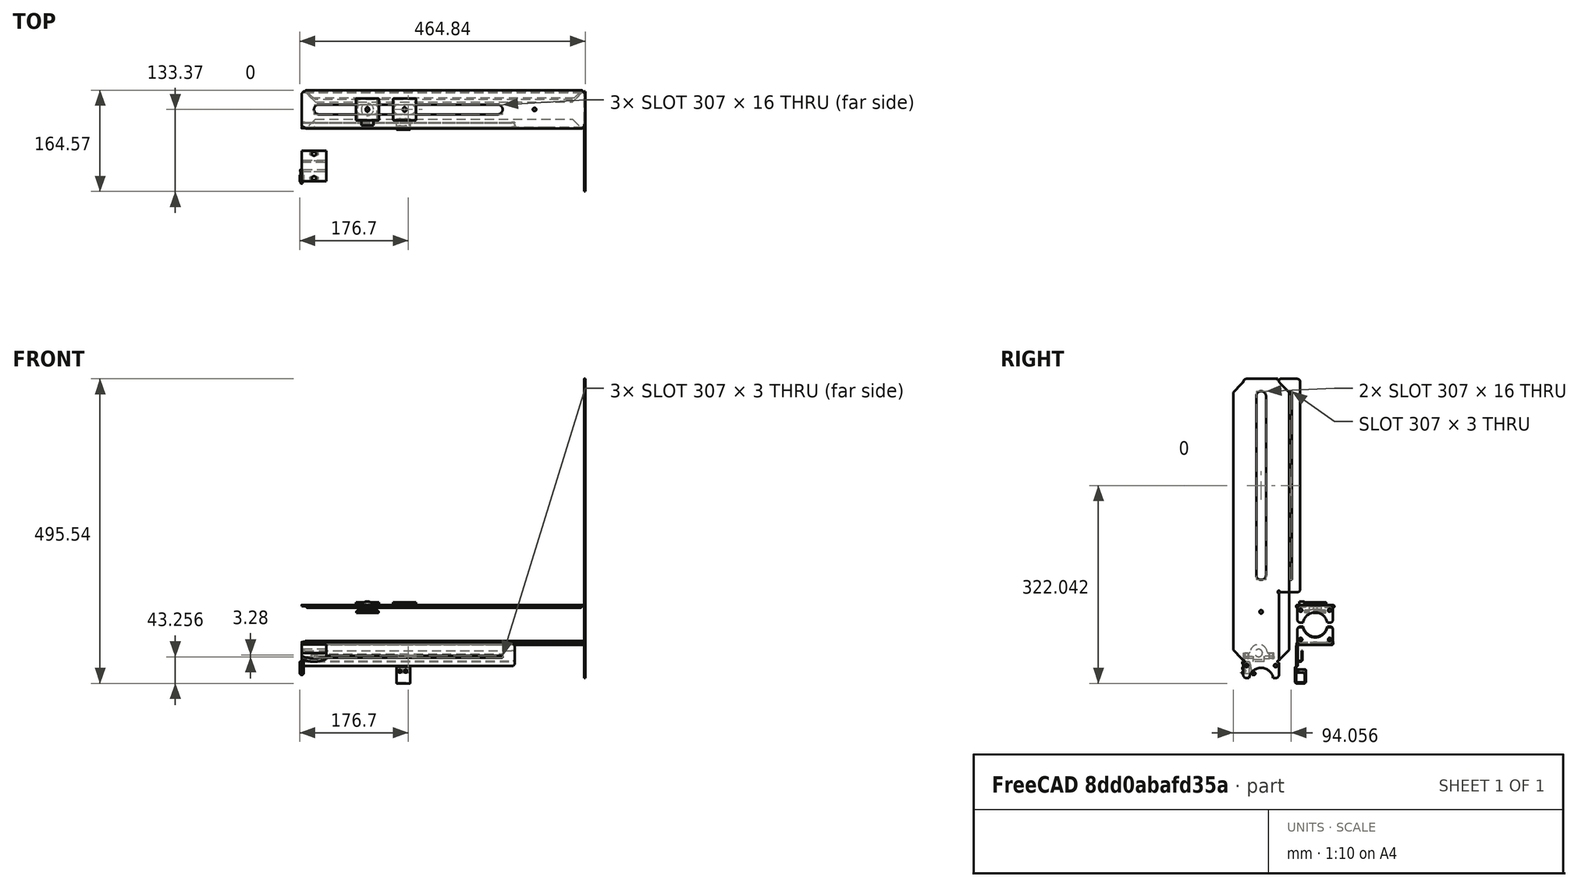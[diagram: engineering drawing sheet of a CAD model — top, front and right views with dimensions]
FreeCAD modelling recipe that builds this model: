
FCSTD DOCUMENT  (FreeCAD 1.0R39285 (Git))
Label: Heberteile
License: All rights reserved
LicenseURL: https://en.wikipedia.org/wiki/All_rights_reserved
objects: Sketcher::SketchObject×33, TechDraw::DrawViewDimension×24, PartDesign::FeaturePython×14, PartDesign::Body×9, PartDesign::Pad×9, Part::Feature×7, PartDesign::Pocket×6, Mesh::Feature×6, TechDraw::DrawProjGroupItem×4, App::DocumentObjectGroup×4, PartDesign::Chamfer×3, PartDesign::Fillet×3, Part::FeaturePython×2, TechDraw::DrawSVGTemplate×2, TechDraw::DrawPage×2, TechDraw::DrawViewImage×1, App::Part×1, PartDesign::Hole×1, PartDesign::SubtractiveLoft×1
note: 223 computed .brp shape members not serialized (recipe doc carries the construction recipe); baked Part::Feature solids carry a one-line shape summary decoded from their .brp

FEATURE [Sketcher::SketchObject] Sketch  label="Sk-Steppersledge-Switch_base"
  ArcFitTolerance = 1e-06
  AttachmentSupport = -> [XY_Plane]
  FullyConstrained = true
  MakeInternals = false
  MapMode = 5
  sketch-geometry (83):
    g0: Circle CenterX=379 CenterY=29 CenterZ=0 NormalX=0 NormalY=0 NormalZ=1 AngleXU=0 Radius=2.75
    g1: ArcOfCircle CenterX=28 CenterY=29 CenterZ=0 NormalX=0 NormalY=0 NormalZ=1 AngleXU=0 Radius=8 StartAngle=1.5708 EndAngle=4.71239
    g2: ArcOfCircle CenterX=319 CenterY=29 CenterZ=0 NormalX=0 NormalY=0 NormalZ=1 AngleXU=0 Radius=8 StartAngle=4.71239 EndAngle=7.85398
    g3: LineSegment StartX=28 StartY=37 StartZ=0 EndX=319 EndY=37 EndZ=0
    g4: LineSegment StartX=28 StartY=21 StartZ=0 EndX=319 EndY=21 EndZ=0
    g5: GeomPoint [constr] X=0 Y=58 Z=0
    g6: ArcOfCircle CenterX=5 CenterY=5 CenterZ=0 NormalX=0 NormalY=0 NormalZ=1 AngleXU=0 Radius=5 StartAngle=3.14159 EndAngle=4.71239
    g7: GeomPoint [constr] X=0 Y=0 Z=0
    g8: LineSegment StartX=487 StartY=48.6914 StartZ=0 EndX=487 EndY=53 EndZ=0
    g9: LineSegment StartX=487 StartY=5 StartZ=0 EndX=487 EndY=9.30863 EndZ=0
    g10: LineSegment [constr] StartX=487 StartY=9.30863 StartZ=0 EndX=487 EndY=48.6914 EndZ=0
    g11: ArcOfCircle CenterX=490.5 CenterY=29 CenterZ=0 NormalX=0 NormalY=0 NormalZ=1 AngleXU=0 Radius=20 StartAngle=1.7467 EndAngle=4.53648
    g12: LineSegment [constr] StartX=490.5 StartY=29 StartZ=0 EndX=487 EndY=29 EndZ=0
    g13: GeomPoint X=20 Y=29 Z=0
    g14: LineSegment StartX=0 StartY=56 StartZ=0 EndX=0 EndY=29 EndZ=0
    g15: LineSegment StartX=0 StartY=29 StartZ=0 EndX=0 EndY=5 EndZ=0
    g16: LineSegment [constr] StartX=460 StartY=58 StartZ=0 EndX=460 EndY=0 EndZ=0
    g17: LineSegment [constr] StartX=490.5 StartY=52.57 StartZ=0 EndX=466.93 EndY=52.57 EndZ=0
    g18: LineSegment [constr] StartX=490.5 StartY=5.43 StartZ=0 EndX=466.93 EndY=5.43 EndZ=0
    g19: LineSegment [constr] StartX=466.93 StartY=52.57 StartZ=0 EndX=466.93 EndY=5.43 EndZ=0
    g20: LineSegment [constr] StartX=490.5 StartY=52.57 StartZ=0 EndX=490.5 EndY=29 EndZ=0
    g21: LineSegment [constr] StartX=490.5 StartY=29 StartZ=0 EndX=490.5 EndY=5.43 EndZ=0
    g22: ArcOfCircle CenterX=482 CenterY=53 CenterZ=0 NormalX=0 NormalY=0 NormalZ=1 AngleXU=0 Radius=5 StartAngle=0 EndAngle=1.5708
    g23: GeomPoint [constr] X=487 Y=58 Z=0
    g24: ArcOfCircle CenterX=482 CenterY=5 CenterZ=0 NormalX=0 NormalY=0 NormalZ=1 AngleXU=0 Radius=5 StartAngle=4.71239 EndAngle=6.28319
    g25: GeomPoint [constr] X=487 Y=0 Z=0
    g26: Circle CenterX=466.93 CenterY=52.57 CenterZ=0 NormalX=0 NormalY=0 NormalZ=1 AngleXU=0 Radius=2.6
    g27: Circle CenterX=466.93 CenterY=5.43 CenterZ=0 NormalX=0 NormalY=0 NormalZ=1 AngleXU=0 Radius=2.6
    g28: LineSegment [constr] StartX=462.83 StartY=50.2029 StartZ=0 EndX=466.93 EndY=47.8357 EndZ=0
    g29: LineSegment [constr] StartX=466.93 StartY=47.8357 StartZ=0 EndX=471.03 EndY=50.2029 EndZ=0
    g30: LineSegment [constr] StartX=471.03 StartY=50.2029 StartZ=0 EndX=471.03 EndY=54.9371 EndZ=0
    g31: LineSegment [constr] StartX=471.03 StartY=54.9371 StartZ=0 EndX=466.93 EndY=57.3043 EndZ=0
    g32: LineSegment [constr] StartX=466.93 StartY=57.3043 StartZ=0 EndX=462.83 EndY=54.9371 EndZ=0
    g33: LineSegment [constr] StartX=462.83 StartY=54.9371 StartZ=0 EndX=462.83 EndY=50.2029 EndZ=0
    g34: Circle [constr] CenterX=466.93 CenterY=52.57 CenterZ=0 NormalX=0 NormalY=0 NormalZ=1 AngleXU=0 Radius=4.73427
    g35: LineSegment StartX=458 StartY=58 StartZ=0 EndX=400 EndY=58 EndZ=0
    g36: LineSegment StartX=482 StartY=58 StartZ=0 EndX=462 EndY=58 EndZ=0
    g37: LineSegment [constr] StartX=462 StartY=58 StartZ=0 EndX=458 EndY=58 EndZ=0
    g38: ArcOfCircle CenterX=460 CenterY=58 CenterZ=0 NormalX=0 NormalY=0 NormalZ=1 AngleXU=0 Radius=2 StartAngle=3.14159 EndAngle=6.28319
    g39: LineSegment StartX=462 StartY=0 StartZ=0 EndX=482 EndY=0 EndZ=0
    g40: LineSegment [constr] StartX=5 StartY=0 StartZ=0 EndX=458 EndY=0 EndZ=0
    g41: LineSegment [constr] StartX=458 StartY=0 StartZ=0 EndX=462 EndY=0 EndZ=0
    g42: ArcOfCircle CenterX=460 CenterY=0 CenterZ=0 NormalX=0 NormalY=0 NormalZ=1 AngleXU=0 Radius=2 StartAngle=0 EndAngle=3.14159
    g43: LineSegment StartX=22 StartY=-17 StartZ=0 EndX=441 EndY=-17 EndZ=0
    g44: LineSegment StartX=441 StartY=-17 StartZ=0 EndX=458 EndY=0 EndZ=0
    g45: LineSegment StartX=22 StartY=-17 StartZ=0 EndX=5 EndY=0 EndZ=0
    g46: LineSegment [constr] StartX=0 StartY=56 StartZ=0 EndX=0 EndY=60 EndZ=0
    g47: LineSegment StartX=5 StartY=93 StartZ=0 EndX=342 EndY=93 EndZ=0
    g48: ArcOfCircle CenterX=5 CenterY=88 CenterZ=0 NormalX=0 NormalY=0 NormalZ=1 AngleXU=0 Radius=5 StartAngle=1.5708 EndAngle=3.14159
    g49: GeomPoint [constr] X=0 Y=93 Z=0
    g50: ArcOfCircle CenterX=342 CenterY=88 CenterZ=0 NormalX=0 NormalY=0 NormalZ=1 AngleXU=0 Radius=5 StartAngle=4e-16 EndAngle=1.5708
    g51: LineSegment StartX=400 StartY=58 StartZ=0 EndX=349 EndY=58 EndZ=0
    g52: LineSegment [constr] StartX=349 StartY=58 StartZ=0 EndX=347 EndY=58 EndZ=0
    g53: ArcOfCircle CenterX=0 CenterY=58 CenterZ=0 NormalX=0 NormalY=0 NormalZ=1 AngleXU=0 Radius=2 StartAngle=4.71239 EndAngle=7.85398
    g54: LineSegment [constr] StartX=347 StartY=60 StartZ=0 EndX=347 EndY=58 EndZ=0
    g55: GeomPoint [constr] X=327 Y=29 Z=0
    g56: LineSegment [constr] StartX=327 StartY=29 StartZ=0 EndX=347 EndY=29 EndZ=0
    g57: LineSegment [constr] StartX=347 StartY=29 StartZ=0 EndX=347 EndY=58 EndZ=0
    g58: LineSegment [constr] StartX=0 StartY=29 StartZ=0 EndX=20 EndY=29 EndZ=0
    g59: LineSegment [constr] StartX=487 StartY=29 StartZ=0 EndX=460 EndY=29 EndZ=0
    g60: LineSegment [constr] StartX=460 StartY=29 StartZ=0 EndX=400 EndY=29 EndZ=0
    g61: LineSegment [constr] StartX=400 StartY=29 StartZ=0 EndX=379 EndY=29 EndZ=0
    g62: LineSegment [constr] StartX=379 StartY=29 StartZ=0 EndX=347 EndY=29 EndZ=0
    g63: LineSegment [constr] StartX=327 StartY=29 StartZ=0 EndX=20 EndY=29 EndZ=0
    g64: LineSegment [constr] StartX=400 StartY=58 StartZ=0 EndX=400 EndY=29 EndZ=0
    g65: LineSegment [constr] StartX=400 StartY=29 StartZ=0 EndX=400 EndY=0 EndZ=0
    g66: LineSegment [constr] StartX=0 StartY=58 StartZ=0 EndX=347 EndY=58 EndZ=0
    g67: ArcOfCircle CenterX=347 CenterY=58 CenterZ=0 NormalX=0 NormalY=0 NormalZ=1 AngleXU=0 Radius=2 StartAngle=1.5708 EndAngle=6.28319
    g68: LineSegment [constr] StartX=28 StartY=29 StartZ=0 EndX=28 EndY=58 EndZ=0
    g69: LineSegment [constr] StartX=28 StartY=58 StartZ=0 EndX=28 EndY=78 EndZ=0
    g70: LineSegment [constr] StartX=28 StartY=78 StartZ=0 EndX=28 EndY=88 EndZ=0
    g71: LineSegment StartX=0 StartY=60 StartZ=0 EndX=0 EndY=88 EndZ=0
    g72: LineSegment StartX=347 StartY=88 StartZ=0 EndX=347 EndY=60 EndZ=0
    g73: LineSegment [constr] StartX=0 StartY=88 StartZ=0 EndX=347 EndY=88 EndZ=0
    g74: LineSegment [constr] StartX=0 StartY=78 StartZ=0 EndX=347 EndY=78 EndZ=0
    g75: ArcOfCircle CenterX=21.5 CenterY=78 CenterZ=0 NormalX=0 NormalY=0 NormalZ=1 AngleXU=0 Radius=1.5 StartAngle=1.5708 EndAngle=4.71239
    g76: ArcOfCircle CenterX=325.5 CenterY=78 CenterZ=0 NormalX=0 NormalY=0 NormalZ=1 AngleXU=0 Radius=1.5 StartAngle=4.71239 EndAngle=7.85398
    g77: LineSegment StartX=21.5 StartY=79.5 StartZ=0 EndX=325.5 EndY=79.5 EndZ=0
    g78: LineSegment StartX=21.5 StartY=76.5 StartZ=0 EndX=325.5 EndY=76.5 EndZ=0
    g79: GeomPoint X=327 Y=78 Z=0
    g80: GeomPoint X=20 Y=78 Z=0
    g81: LineSegment [constr] StartX=20 StartY=78 StartZ=0 EndX=20 EndY=29 EndZ=0
    g82: LineSegment [constr] StartX=327 StartY=78 StartZ=0 EndX=327 EndY=29 EndZ=0
  constraints (211):
    c: Diameter(g0) = 5.5
    c: Tangent(g1,g3) = 1.5708
    c: Tangent(g1,g4) = -1.5708
    c: Tangent(g2,g3) = 1.5708
    c: Tangent(g2,g4) = -1.5708
    c: Equal(g1,g2)
    c: Horizontal(g4)
    c: Coincident(g35,g51)
    c: DistanceY(g65,g64) = 58
    c: Coincident(g35,g64)
    c: Coincident(g10,g8)
    c: Vertical(g8)
    c: Coincident(g9,g10)
    c: Vertical(g9)
    c: Vertical(g10)
    c: Coincident(g11,g8)
    c: Coincident(g11,g9)
    c: Coincident(g12,g11)
    c: Horizontal(g12)
    c: Radius(g11) = 20
    c: DistanceX(g12,g12) = 3.5
    c: DistanceX(g15,g65) = 400
    c: Coincident(g14,g15)
    c: PointOnObject(g7,g14)
    c: DistanceX(g14,g13) = 20
    c: Vertical(g14)
    c: Tangent(g15,g6) = -1.5708
    c: Vertical(g15)
    c: DistanceX(g0,g65) = 21
    c: DistanceX(g2,g0) = 60
    c: Vertical(g16)
    c: DistanceX(g65,g16) = 60
    c: Coincident(g17,g20)
    c: Horizontal(g17)
    c: Coincident(g18,g21)
    c: Horizontal(g18)
    c: Coincident(g19,g17)
    c: Coincident(g19,g18)
    c: Vertical(g19)
    c: Coincident(g20,g21)
    c: Vertical(g20)
    c: Vertical(g21)
    c: Equal(g20,g21)
    c: DistanceY(g18,g17) = 47.14
    c: Equal(g20,g17)
    c: PointOnObject(g23,g8)
    c: Tangent(g8,g22) = -1.5708
    c: PointOnObject(g25,g9)
    c: Tangent(g9,g24) = -1.5708
    c: Equal(g24,g22)
    c: DistanceX(g16,g18) = 30.5
    c: Coincident(g26,g17)
    c: Diameter(g26) = 5.2
    c: Coincident(g27,g18)
    c: Equal(g26,g27)
    c: Coincident(g28,g29)
    c: Coincident(g29,g30)
    c: Coincident(g30,g31)
    c: Coincident(g31,g32)
    c: Coincident(g32,g33)
    c: Coincident(g33,g28)
    c: Equal(g28, g29-g33) x5
    c: PointOnObject(g28,g34)
    c: PointOnObject(g29,g34)
    c: PointOnObject(g30,g34)
    c: PointOnObject(g31,g34)
    c: PointOnObject(g32,g34)
    c: PointOnObject(g33,g34)
    c: Coincident(g34,g17)
    c: Vertical(g33)
    c: DistanceX(g32,g30) = 8.2
    c: Radius(g2) = 8
    c: Coincident(g37,g35)
    c: Horizontal(g35)
    c: Coincident(g36,g37)
    c: Horizontal(g36)
    c: Horizontal(g37)
    c: PointOnObject(g16,g36)
    c: PointOnObject(g23,g36)
    c: Coincident(g38,g16)
    c: Coincident(g38,g35)
    c: Coincident(g38,g36)
    c: Radius(g38) = 2
    c: Tangent(g36,g22) = -1.5708
    c: Coincident(g41,g39)
    c: Horizontal(g39)
    c: PointOnObject(g65,g39)
    c: PointOnObject(g16,g39)
    c: PointOnObject(g25,g39)
    c: Coincident(g40,g41)
    c: Horizontal(g40)
    c: Horizontal(g41)
    c: PointOnObject(g7,g40)
    c: Coincident(g42,g16)
    c: Coincident(g42,g39)
    c: Coincident(g42,g40)
    c: Tangent(g39,g24) = -1.5708
    c: Equal(g42,g38)
    c: Tangent(g40,g6) = -1.5708
    c: Horizontal(g43)
    c: Coincident(g43,g44)
    c: Coincident(g44,g40)
    c: Coincident(g45,g43)
    c: Coincident(g45,g6)
    c: Angle(g45,g40) = 0.785398
    c: Equal(g45,g44)
    c: DistanceY(g43,g6) = 17
    c: Vertical(g46)
    c: Coincident(g46,g71)
    c: Horizontal(g47)
    c: Radius(g6) = 5
    c: PointOnObject(g49,g47)
    c: Tangent(g47,g48) = 1.5708
    c: Tangent(g47,g50) = 1.5708
    c: Coincident(g51,g52)
    c: Horizontal(g51)
    c: Horizontal(g52)
    c: Equal(g6,g48)
    c: Equal(g48,g50)
    c: Coincident(g14,g46)
    c: Coincident(g53,g5)
    c: Coincident(g53,g14)
    c: Coincident(g53,g46)
    c: Coincident(g56,g55)
    c: Coincident(g57,g56)
    c: Vertical(g57)
    c: Coincident(g58,g14)
    c: Coincident(g58,g13)
    c: Equal(g58,g56)
    c: PointOnObject(g5,g46)
    c: Horizontal(g56)
    c: Coincident(g11,g20)
    c: Coincident(g59,g12)
    c: PointOnObject(g59,g16)
    c: Horizontal(g59)
    c: Coincident(g60,g59)
    c: Horizontal(g60)
    c: Coincident(g61,g60)
    c: Coincident(g61,g0)
    c: Coincident(g62,g0)
    c: Coincident(g62,g56)
    c: Horizontal(g62)
    c: Horizontal(g61)
    c: Coincident(g63,g55)
    c: PointOnObject(g63,g1)
    c: Horizontal(g63)
    c: Coincident(g13,g63)
    c: PointOnObject(g1,g63)
    c: Horizontal(g58)
    c: PointOnObject(g55,g2)
    c: PointOnObject(g12,g10)
    c: Coincident(g64,g65)
    c: Vertical(g64)
    c: Vertical(g65)
    c: Coincident(g64,g60)
    c: Equal(g64,g65)
    c: Equal(g24,g6)
    c: Coincident(g66,g5)
    c: Horizontal(g66)
    c: Vertical(g54)
    c: Coincident(g57,g54)
    c: Coincident(g52,g54)
    c: Coincident(g72,g54)
    c: Coincident(g66,g52)
    c: Coincident(g67,g52)
    c: Coincident(g67,g54)
    c: Coincident(g67,g51)
    c: Equal(g53,g67)
    c: Equal(g67,g38)
    c: Coincident(g7,g-1)
    c: Coincident(g68,g1)
    c: PointOnObject(g68,g66)
    c: Vertical(g68)
    c: Coincident(g69,g68)
    c: Vertical(g69)
    c: Coincident(g70,g69)
    c: Vertical(g70)
    c: DistanceY(g69,g69) = 20
    c: DistanceY(g70,g70) = 10
    c: Vertical(g71)
    c: PointOnObject(g49,g71)
    c: Vertical(g72)
    c: Horizontal(g73)
    c: PointOnObject(g70,g73)
    c: PointOnObject(g74,g71)
    c: PointOnObject(g74,g72)
    c: Horizontal(g74)
    c: PointOnObject(g69,g74)
    c: Tangent(g75,g77) = 1.5708
    c: Tangent(g75,g78) = -1.5708
    c: Tangent(g76,g77) = 1.5708
    c: Tangent(g76,g78) = -1.5708
    c: Equal(g75,g76)
    c: Horizontal(g78)
    c: Radius(g75) = 1.5
    c: PointOnObject(g75,g74)
    c: PointOnObject(g79,g74)
    c: PointOnObject(g79,g76)
    c: PointOnObject(g80,g74)
    c: PointOnObject(g80,g75)
    c: Coincident(g81,g80)
    c: Coincident(g81,g13)
    c: Coincident(g82,g79)
    c: Coincident(g82,g55)
    c: Vertical(g82)
    c: DistanceX(g56,g56) = 20
    c: Coincident(g71,g73)
    c: Tangent(g48,g71) = 1.5708
    c: Coincident(g73,g72)
    c: Coincident(g73,g50)
    c: Vertical(g81)
FEATURE [PartDesign::FeaturePython] BaseBend  label="S-Steppersledge-Switch_base"  # WARN: FeaturePython — macro-defined, semantics opaque (R4)
  BendSide = 0
  BendSketch = -> Sketch
  Length = 100
  MidPlane = false
  Radius = 2
  Reverse = false
  Suppressed = false
  Thickness = 2
FEATURE [Sketcher::SketchObject] Sketch001  label="Sk-SsSw_Bendline_Steppermount"
  ArcFitTolerance = 1e-06
  AttachmentSupport = -> [BaseBend]
  ExternalGeometry = -> [BaseBend]
  FullyConstrained = true
  MakeInternals = false
  MapMode = 5
  Placement = pos=(0,0,0) rot=(1,0,0;3.14159rad)
  sketch-geometry (1):
    g0: LineSegment StartX=460 StartY=-58 StartZ=0 EndX=460 EndY=0 EndZ=0
  constraints (2):
    c: Coincident(g0,g-4)
    c: Coincident(g-3,g0)
FEATURE [PartDesign::FeaturePython] Fold  label="Fd-Steppersledge-Sw-Mount"  # WARN: FeaturePython — macro-defined, semantics opaque (R4)
  BaseFeature = -> BaseBend
  BendLine = -> Sketch001
  Position = 1
  Suppressed = false
  angle = 90
  baseObject = -> BaseBend [Face36]
  invert = false
  invertbend = false
  kfactor = 0.5
  radius = 2
  unfold = false
FEATURE [Sketcher::SketchObject] Sketch002  label="Sk-SsSw_Bendline-Seam-Bottom"
  ArcFitTolerance = 1e-06
  AttachmentSupport = -> [Fold]
  ExternalGeometry = -> [Fold]
  FullyConstrained = true
  MakeInternals = false
  MapMode = 5
  Placement = pos=(0,0,0) rot=(1,0,0;3.14159rad)
  sketch-geometry (2):
    g0: LineSegment StartX=0 StartY=0 StartZ=0 EndX=459.644 EndY=0 EndZ=0
    g1: LineSegment [constr] StartX=0 StartY=0 StartZ=0 EndX=0 EndY=-5 EndZ=0
  constraints (5):
    c: Horizontal(g0)
    c: Coincident(g1,g0)
    c: Coincident(g1,g-3)
    c: Vertical(g1)
    c: Coincident(g0,g-4)
FEATURE [PartDesign::FeaturePython] Fold001  label="Fd-Steppersledge-Sw-Seam"  # WARN: FeaturePython — macro-defined, semantics opaque (R4)
  BaseFeature = -> Fold
  BendLine = -> Sketch002
  Position = 1
  Suppressed = false
  angle = 181
  baseObject = -> Fold [Face4]
  invert = false
  invertbend = false
  kfactor = 0.5
  radius = 0.2
  unfold = false
FEATURE [Sketcher::SketchObject] Sketch006  label="Sk-SsSw_Bendline-Switchprofile_3"
  ArcFitTolerance = 1e-06
  AttachmentSupport = -> [Fold001]
  ExternalGeometry = -> [Fold001]
  FullyConstrained = true
  MakeInternals = false
  MapMode = 5
  Placement = pos=(0,0,2) rot=(0,0,1;0rad)
  sketch-geometry (1):
    g0: LineSegment StartX=0 StartY=58 StartZ=0 EndX=347 EndY=58 EndZ=0
  constraints (2):
    c: Coincident(g0,g-3)
    c: Coincident(g0,g-4)
FEATURE [Sketcher::SketchObject] Sketch007  label="Sk-Steppersledge-basic_base"
  ArcFitTolerance = 1e-06
  AttachmentSupport = -> [XY_Plane002]
  FullyConstrained = true
  MakeInternals = false
  MapMode = 5
  sketch-geometry (62):
    g0: Circle CenterX=379 CenterY=29 CenterZ=0 NormalX=0 NormalY=0 NormalZ=1 AngleXU=0 Radius=2.75
    g1: ArcOfCircle CenterX=28 CenterY=29 CenterZ=0 NormalX=0 NormalY=0 NormalZ=1 AngleXU=0 Radius=8 StartAngle=1.5708 EndAngle=4.71239
    g2: ArcOfCircle CenterX=319 CenterY=29 CenterZ=0 NormalX=0 NormalY=0 NormalZ=1 AngleXU=0 Radius=8 StartAngle=4.71239 EndAngle=7.85398
    g3: LineSegment StartX=28 StartY=37 StartZ=0 EndX=319 EndY=37 EndZ=0
    g4: LineSegment StartX=28 StartY=21 StartZ=0 EndX=319 EndY=21 EndZ=0
    g5: GeomPoint [constr] X=5 Y=58 Z=0
    g6: ArcOfCircle CenterX=5 CenterY=5 CenterZ=0 NormalX=0 NormalY=0 NormalZ=1 AngleXU=0 Radius=5 StartAngle=3.14159 EndAngle=4.71239
    g7: GeomPoint [constr] X=0 Y=0 Z=0
    g8: LineSegment StartX=487 StartY=48.6914 StartZ=0 EndX=487 EndY=53 EndZ=0
    g9: LineSegment StartX=487 StartY=5 StartZ=0 EndX=487 EndY=9.30863 EndZ=0
    g10: LineSegment [constr] StartX=487 StartY=9.30863 StartZ=0 EndX=487 EndY=48.6914 EndZ=0
    g11: ArcOfCircle CenterX=490.5 CenterY=29 CenterZ=0 NormalX=0 NormalY=0 NormalZ=1 AngleXU=0 Radius=20 StartAngle=1.7467 EndAngle=4.53648
    g12: LineSegment [constr] StartX=490.5 StartY=29 StartZ=0 EndX=487 EndY=29 EndZ=0
    g13: GeomPoint X=20 Y=29 Z=0
    g14: LineSegment StartX=0 StartY=53 StartZ=0 EndX=0 EndY=29 EndZ=0
    g15: LineSegment StartX=0 StartY=29 StartZ=0 EndX=0 EndY=5 EndZ=0
    g16: LineSegment [constr] StartX=460 StartY=58 StartZ=0 EndX=460 EndY=0 EndZ=0
    g17: LineSegment [constr] StartX=490.5 StartY=52.57 StartZ=0 EndX=466.93 EndY=52.57 EndZ=0
    g18: LineSegment [constr] StartX=490.5 StartY=5.43 StartZ=0 EndX=466.93 EndY=5.43 EndZ=0
    g19: LineSegment [constr] StartX=466.93 StartY=52.57 StartZ=0 EndX=466.93 EndY=5.43 EndZ=0
    g20: LineSegment [constr] StartX=490.5 StartY=52.57 StartZ=0 EndX=490.5 EndY=29 EndZ=0
    g21: LineSegment [constr] StartX=490.5 StartY=29 StartZ=0 EndX=490.5 EndY=5.43 EndZ=0
    g22: ArcOfCircle CenterX=482 CenterY=53 CenterZ=0 NormalX=0 NormalY=0 NormalZ=1 AngleXU=0 Radius=5 StartAngle=0 EndAngle=1.5708
    g23: GeomPoint [constr] X=487 Y=58 Z=0
    g24: ArcOfCircle CenterX=482 CenterY=5 CenterZ=0 NormalX=0 NormalY=0 NormalZ=1 AngleXU=0 Radius=5 StartAngle=4.71239 EndAngle=6.28319
    g25: GeomPoint [constr] X=487 Y=0 Z=0
    g26: Circle CenterX=466.93 CenterY=52.57 CenterZ=0 NormalX=0 NormalY=0 NormalZ=1 AngleXU=0 Radius=2.6
    g27: Circle CenterX=466.93 CenterY=5.43 CenterZ=0 NormalX=0 NormalY=0 NormalZ=1 AngleXU=0 Radius=2.6
    g28: LineSegment [constr] StartX=462.83 StartY=50.2029 StartZ=0 EndX=466.93 EndY=47.8357 EndZ=0
    g29: LineSegment [constr] StartX=466.93 StartY=47.8357 StartZ=0 EndX=471.03 EndY=50.2029 EndZ=0
    g30: LineSegment [constr] StartX=471.03 StartY=50.2029 StartZ=0 EndX=471.03 EndY=54.9371 EndZ=0
    g31: LineSegment [constr] StartX=471.03 StartY=54.9371 StartZ=0 EndX=466.93 EndY=57.3043 EndZ=0
    g32: LineSegment [constr] StartX=466.93 StartY=57.3043 StartZ=0 EndX=462.83 EndY=54.9371 EndZ=0
    g33: LineSegment [constr] StartX=462.83 StartY=54.9371 StartZ=0 EndX=462.83 EndY=50.2029 EndZ=0
    g34: Circle [constr] CenterX=466.93 CenterY=52.57 CenterZ=0 NormalX=0 NormalY=0 NormalZ=1 AngleXU=0 Radius=4.73427
    g35: LineSegment [constr] StartX=458 StartY=58 StartZ=0 EndX=400 EndY=58 EndZ=0
    g36: LineSegment StartX=482 StartY=58 StartZ=0 EndX=462 EndY=58 EndZ=0
    g37: LineSegment [constr] StartX=462 StartY=58 StartZ=0 EndX=458 EndY=58 EndZ=0
    g38: ArcOfCircle CenterX=460 CenterY=58 CenterZ=0 NormalX=0 NormalY=0 NormalZ=1 AngleXU=0 Radius=2 StartAngle=3.14159 EndAngle=6.28319
    g39: LineSegment StartX=462 StartY=0 StartZ=0 EndX=482 EndY=0 EndZ=0
    g40: LineSegment [constr] StartX=5 StartY=0 StartZ=0 EndX=458 EndY=0 EndZ=0
    g41: LineSegment [constr] StartX=458 StartY=0 StartZ=0 EndX=462 EndY=0 EndZ=0
    g42: ArcOfCircle CenterX=460 CenterY=0 CenterZ=0 NormalX=0 NormalY=0 NormalZ=1 AngleXU=0 Radius=2 StartAngle=0 EndAngle=3.14159
    g43: LineSegment StartX=22 StartY=-17 StartZ=0 EndX=441 EndY=-17 EndZ=0
    g44: LineSegment StartX=441 StartY=-17 StartZ=0 EndX=458 EndY=0 EndZ=0
    g45: LineSegment StartX=22 StartY=-17 StartZ=0 EndX=5 EndY=0 EndZ=0
    g46: GeomPoint [constr] X=327 Y=29 Z=0
    g47: LineSegment [constr] StartX=327 StartY=29 StartZ=0 EndX=347 EndY=29 EndZ=0
    g48: LineSegment [constr] StartX=0 StartY=29 StartZ=0 EndX=20 EndY=29 EndZ=0
    g49: LineSegment [constr] StartX=487 StartY=29 StartZ=0 EndX=460 EndY=29 EndZ=0
    g50: LineSegment [constr] StartX=460 StartY=29 StartZ=0 EndX=400 EndY=29 EndZ=0
    g51: LineSegment [constr] StartX=400 StartY=29 StartZ=0 EndX=379 EndY=29 EndZ=0
    g52: LineSegment [constr] StartX=379 StartY=29 StartZ=0 EndX=347 EndY=29 EndZ=0
    g53: LineSegment [constr] StartX=327 StartY=29 StartZ=0 EndX=20 EndY=29 EndZ=0
    g54: LineSegment [constr] StartX=400 StartY=58 StartZ=0 EndX=400 EndY=29 EndZ=0
    g55: LineSegment [constr] StartX=400 StartY=29 StartZ=0 EndX=400 EndY=0 EndZ=0
    g56: LineSegment [constr] StartX=5 StartY=58 StartZ=0 EndX=400 EndY=58 EndZ=0
    g57: LineSegment [constr] StartX=28 StartY=29 StartZ=0 EndX=28 EndY=58 EndZ=0
    g58: LineSegment StartX=458 StartY=58 StartZ=0 EndX=441 EndY=75 EndZ=0
    g59: LineSegment StartX=441 StartY=75 StartZ=0 EndX=22 EndY=75 EndZ=0
    g60: LineSegment StartX=22 StartY=75 StartZ=0 EndX=5 EndY=58 EndZ=0
    g61: ArcOfCircle CenterX=5 CenterY=53 CenterZ=0 NormalX=0 NormalY=0 NormalZ=1 AngleXU=0 Radius=5 StartAngle=1.5708 EndAngle=3.14159
  constraints (157):
    c: Diameter(g0) = 5.5
    c: Tangent(g1,g3) = 1.5708
    c: Tangent(g1,g4) = -1.5708
    c: Tangent(g2,g3) = 1.5708
    c: Tangent(g2,g4) = -1.5708
    c: Equal(g1,g2)
    c: Horizontal(g4)
    c: DistanceY(g55,g54) = 58
    c: Coincident(g35,g54)
    c: Coincident(g10,g8)
    c: Vertical(g8)
    c: Coincident(g9,g10)
    c: Vertical(g9)
    c: Vertical(g10)
    c: Coincident(g11,g8)
    c: Coincident(g11,g9)
    c: Coincident(g12,g11)
    c: Horizontal(g12)
    c: Radius(g11) = 20
    c: DistanceX(g12,g12) = 3.5
    c: DistanceX(g15,g55) = 400
    c: Coincident(g14,g15)
    c: PointOnObject(g7,g14)
    c: DistanceX(g14,g13) = 20
    c: Vertical(g14)
    c: Tangent(g15,g6) = -1.5708
    c: Vertical(g15)
    c: DistanceX(g0,g55) = 21
    c: DistanceX(g2,g0) = 60
    c: Vertical(g16)
    c: DistanceX(g55,g16) = 60
    c: Coincident(g17,g20)
    c: Horizontal(g17)
    c: Coincident(g18,g21)
    c: Horizontal(g18)
    c: Coincident(g19,g17)
    c: Coincident(g19,g18)
    c: Vertical(g19)
    c: Coincident(g20,g21)
    c: Vertical(g20)
    c: Vertical(g21)
    c: Equal(g20,g21)
    c: DistanceY(g18,g17) = 47.14
    c: Equal(g20,g17)
    c: PointOnObject(g23,g8)
    c: Tangent(g8,g22) = -1.5708
    c: PointOnObject(g25,g9)
    c: Tangent(g9,g24) = -1.5708
    c: Equal(g24,g22)
    c: DistanceX(g16,g18) = 30.5
    c: Coincident(g26,g17)
    c: Diameter(g26) = 5.2
    c: Coincident(g27,g18)
    c: Equal(g26,g27)
    c: Coincident(g28,g29)
    c: Coincident(g29,g30)
    c: Coincident(g30,g31)
    c: Coincident(g31,g32)
    c: Coincident(g32,g33)
    c: Coincident(g33,g28)
    c: Equal(g28, g29-g33) x5
    c: PointOnObject(g28,g34)
    c: PointOnObject(g29,g34)
    c: PointOnObject(g30,g34)
    c: PointOnObject(g31,g34)
    c: PointOnObject(g32,g34)
    c: PointOnObject(g33,g34)
    c: Coincident(g34,g17)
    c: Vertical(g33)
    c: DistanceX(g32,g30) = 8.2
    c: Radius(g2) = 8
    c: Coincident(g37,g35)
    c: Horizontal(g35)
    c: Coincident(g36,g37)
    c: Horizontal(g36)
    c: Horizontal(g37)
    c: PointOnObject(g16,g36)
    c: PointOnObject(g23,g36)
    c: Coincident(g38,g16)
    c: Coincident(g38,g35)
    c: Coincident(g38,g36)
    c: Radius(g38) = 2
    c: Tangent(g36,g22) = -1.5708
    c: Coincident(g41,g39)
    c: Horizontal(g39)
    c: PointOnObject(g55,g39)
    c: PointOnObject(g16,g39)
    c: PointOnObject(g25,g39)
    c: Coincident(g40,g41)
    c: Horizontal(g40)
    c: Horizontal(g41)
    c: PointOnObject(g7,g40)
    c: Coincident(g42,g16)
    c: Coincident(g42,g39)
    c: Coincident(g42,g40)
    c: Tangent(g39,g24) = -1.5708
    c: Equal(g42,g38)
    c: Tangent(g40,g6) = -1.5708
    c: Horizontal(g43)
    c: Coincident(g43,g44)
    c: Coincident(g44,g40)
    c: Coincident(g45,g43)
    c: Coincident(g45,g6)
    c: Angle(g45,g40) = 0.785398
    c: Equal(g45,g44)
    c: DistanceY(g43,g6) = 17
    c: Radius(g6) = 5
    c: Coincident(g47,g46)
    c: Coincident(g48,g14)
    c: Coincident(g48,g13)
    c: Equal(g48,g47)
    c: Horizontal(g47)
    c: Coincident(g11,g20)
    c: Coincident(g49,g12)
    c: PointOnObject(g49,g16)
    c: Horizontal(g49)
    c: Coincident(g50,g49)
    c: Horizontal(g50)
    c: Coincident(g51,g50)
    c: Coincident(g51,g0)
    c: Coincident(g52,g0)
    c: Coincident(g52,g47)
    c: Horizontal(g52)
    c: Horizontal(g51)
    c: Coincident(g53,g46)
    c: PointOnObject(g53,g1)
    c: Horizontal(g53)
    c: Coincident(g13,g53)
    c: PointOnObject(g1,g53)
    c: Horizontal(g48)
    c: PointOnObject(g46,g2)
    c: PointOnObject(g12,g10)
    c: Coincident(g54,g55)
    c: Vertical(g54)
    c: Vertical(g55)
    c: Coincident(g54,g50)
    c: Equal(g54,g55)
    c: Equal(g24,g6)
    c: Coincident(g56,g5)
    c: Horizontal(g56)
    c: Coincident(g7,g-1)
    c: Coincident(g57,g1)
    c: PointOnObject(g57,g56)
    c: Vertical(g57)
    c: Coincident(g56,g35)
    c: Coincident(g35,g58)
    c: Coincident(g58,g59)
    c: Horizontal(g59)
    c: Coincident(g59,g60)
    c: Coincident(g61,g5)
    c: Tangent(g61,g14) = -1.5708
    c: Tangent(g61,g56)
    c: Equal(g6,g61)
    c: Coincident(g60,g5)
    c: Equal(g45,g60)
    c: Equal(g60,g58)
    c: Angle(g56,g60) = 0.785398
FEATURE [PartDesign::FeaturePython] BaseBend001  label="S-Steppersledge-basic_base"  # WARN: FeaturePython — macro-defined, semantics opaque (R4)
  BendSide = 0
  BendSketch = -> Sketch007
  Length = 100
  MidPlane = false
  Radius = 2
  Reverse = false
  Suppressed = false
  Thickness = 2
FEATURE [Sketcher::SketchObject] Sketch008  label="Sk-Ssb_Bendline_Steppermount"
  ArcFitTolerance = 1e-06
  AttachmentSupport = -> [BaseBend001]
  ExternalGeometry = -> [BaseBend001]
  FullyConstrained = true
  MakeInternals = false
  MapMode = 5
  Placement = pos=(0,0,0) rot=(1,0,0;3.14159rad)
  sketch-geometry (1):
    g0: LineSegment StartX=460 StartY=-58 StartZ=0 EndX=460 EndY=0 EndZ=0
  constraints (2):
    c: Coincident(g0,g-4)
    c: Coincident(g-3,g0)
FEATURE [PartDesign::FeaturePython] Fold005  label="Fd-Steppersledge-basic_Mount"  # WARN: FeaturePython — macro-defined, semantics opaque (R4)
  BaseFeature = -> BaseBend001
  BendLine = -> Sketch008
  Position = 1
  Suppressed = false
  angle = 90
  baseObject = -> BaseBend001 [Face27]
  invert = false
  invertbend = false
  kfactor = 0.5
  radius = 2
  unfold = false
FEATURE [Sketcher::SketchObject] Sketch009  label="Sk-Ssb_Bendline-Seam-Bottom"
  ArcFitTolerance = 1e-06
  AttachmentSupport = -> [Fold005]
  ExternalGeometry = -> [Fold005]
  FullyConstrained = true
  MakeInternals = false
  MapMode = 5
  Placement = pos=(0,0,0) rot=(1,0,0;3.14159rad)
  sketch-geometry (2):
    g0: LineSegment StartX=0 StartY=0 StartZ=0 EndX=461.644 EndY=0 EndZ=0
    g1: LineSegment [constr] StartX=0 StartY=0 StartZ=0 EndX=0 EndY=-5 EndZ=0
  constraints (5):
    c: Horizontal(g0)
    c: Coincident(g1,g0)
    c: Vertical(g1)
    c: Coincident(g0,g-4)
    c: Coincident(g1,g-3)
FEATURE [PartDesign::FeaturePython] Fold006  label="Fd-Steppersledge-basic_Seam"  # WARN: FeaturePython — macro-defined, semantics opaque (R4)
  BaseFeature = -> Fold005
  BendLine = -> Sketch009
  Position = 3
  Suppressed = false
  angle = 181
  baseObject = -> Fold005 [Face3]
  invert = false
  invertbend = false
  kfactor = 0.5
  radius = 0.2
  unfold = false
FEATURE [Sketcher::SketchObject] Sketch010  label="Sk-Ssb_Bendline-Seam-Top"
  ArcFitTolerance = 1e-06
  AttachmentSupport = -> [Fold006]
  ExternalGeometry = -> [Fold006]
  FullyConstrained = true
  MakeInternals = false
  MapMode = 5
  Placement = pos=(0,0,0) rot=(1,0,0;3.14159rad)
  sketch-geometry (1):
    g0: LineSegment StartX=5 StartY=-58 StartZ=0 EndX=458 EndY=-58 EndZ=0
  constraints (2):
    c: Coincident(g0,g-3)
    c: Coincident(g0,g-4)
FEATURE [PartDesign::FeaturePython] Fold007  label="Fd-Steppersledge basic_complete"  # WARN: FeaturePython — macro-defined, semantics opaque (R4)
  BaseFeature = -> Fold006
  BendLine = -> Sketch010
  Position = 3
  Suppressed = false
  angle = 181
  baseObject = -> Fold006 [?Face2]
  invert = false
  invertbend = false
  kfactor = 0.5
  radius = 0.2
  unfold = false
FEATURE [PartDesign::Body] Body001  label="B-Steppersledge basic"
  AllowCompound = false
  Group = -> [Sketch007,BaseBend001,Fold005,Fold006,Fold007]
  Origin = -> Origin002
  Placement = pos=(0,88,90.1) rot=(0,0,1;0rad)
  Tip = -> Fold007
FEATURE [Part::FeaturePython] Body001_Unfold  label="B-Steppersledge basic_Unfold"  # WARN: FeaturePython — macro-defined, semantics opaque (R4)
  GenerateSketch = false
  KFactor = 0.4
  KFactorStandard = 0
  ManualRecompute = false
  MaterialSheet = _manual
  SeparateSketchLayers = true
  baseObject = -> Body001 [Fold007.Face29]
FEATURE [TechDraw::DrawSVGTemplate] Template001  label="Vorlage001"
  EditableTexts = AUTHOR_NAME=Unseen Obstacles; DN=01; DRAWING_TITLE=Mover Stepper Mounts; FC-DATE=20/10/2025; FC-REV=r 01.10; FC-SC=1 : 2; FC-SH=1 / 1; FC-SI=A4; FreeCAD_DRAWING=Bend Radius: 2 mm; PN=01; SI-1=Material: 2 mm Steel Sheet; SI-3=CNC Template
  Height = 210
  Orientation = 1
  Template = <path>
  Width = 297
FEATURE [Sketcher::SketchObject] Sketch011  label="Sk-Mount Washer"
  ArcFitTolerance = 1e-06
  AttachmentSupport = -> [XY_Plane004]
  FullyConstrained = true
  MakeInternals = false
  MapMode = 5
  sketch-geometry (2):
    g0: Circle CenterX=0 CenterY=0 CenterZ=0 NormalX=0 NormalY=0 NormalZ=1 AngleXU=0 Radius=2.75
    g1: Circle CenterX=0 CenterY=0 CenterZ=0 NormalX=0 NormalY=0 NormalZ=1 AngleXU=0 Radius=10
  constraints (4):
    c: Coincident(g0,g-1)
    c: Diameter(g0) = 5.5
    c: Diameter(g1) = 20
    c: Coincident(g1,g0)
FEATURE [PartDesign::Pad] Pad  label="P-Mount Washer"
  Direction = (0,0,1)
  Length = 4
  Length2 = 10
  Profile = -> Sketch011
  ReferenceAxis = -> Sketch011 [N_Axis]
  Refine = true
  Suppressed = false
  Type = 0
FEATURE [PartDesign::Body] Body002  label="B-Mount Washer"
  AllowCompound = false
  Group = -> [Sketch011,Pad]
  Origin = -> Origin004
  Placement = pos=(106.9,116.9,85.2) rot=(0,0,1;0rad)
  Tip = -> Pad
FEATURE [Sketcher::SketchObject] Sketch012  label="Sk-SlideBearing_Shaft"
  ArcFitTolerance = 1e-06
  AttachmentSupport = -> [XY_Plane005]
  FullyConstrained = true
  MakeInternals = false
  MapMode = 5
  sketch-geometry (12):
    g0: ArcOfCircle CenterX=-10 CenterY=0 CenterZ=0 NormalX=0 NormalY=0 NormalZ=1 AngleXU=0 Radius=7.7 StartAngle=1.5708 EndAngle=4.71239
    g1: ArcOfCircle CenterX=10 CenterY=2e-16 CenterZ=0 NormalX=0 NormalY=0 NormalZ=1 AngleXU=0 Radius=7.7 StartAngle=4.71239 EndAngle=7.85398
    g2: LineSegment StartX=-10 StartY=7.7 StartZ=0 EndX=10 EndY=7.7 EndZ=0
    g3: LineSegment StartX=-10 StartY=-7.7 StartZ=0 EndX=10 EndY=-7.7 EndZ=0
    g4: ArcOfCircle CenterX=0 CenterY=1 CenterZ=0 NormalX=0 NormalY=0 NormalZ=1 AngleXU=0 Radius=2.7 StartAngle=1e-16 EndAngle=3.14159
    g5: ArcOfCircle CenterX=0 CenterY=-1 CenterZ=0 NormalX=0 NormalY=0 NormalZ=1 AngleXU=0 Radius=2.7 StartAngle=3.14159 EndAngle=6.28319
    g6: LineSegment StartX=2.7 StartY=1 StartZ=0 EndX=2.7 EndY=-1 EndZ=0
    g7: LineSegment StartX=-2.7 StartY=1 StartZ=0 EndX=-2.7 EndY=-1 EndZ=0
    g8: LineSegment [constr] StartX=0 StartY=1 StartZ=0 EndX=0 EndY=0 EndZ=0
    g9: LineSegment [constr] StartX=0 StartY=0 StartZ=0 EndX=0 EndY=-1 EndZ=0
    g10: LineSegment [constr] StartX=-10 StartY=0 StartZ=0 EndX=0 EndY=0 EndZ=0
    g11: LineSegment [constr] StartX=0 StartY=0 StartZ=0 EndX=10 EndY=2e-16 EndZ=0
  constraints (28):
    c: Tangent(g0,g2) = 1.5708
    c: Tangent(g0,g3) = -1.5708
    c: Tangent(g1,g2) = 1.5708
    c: Tangent(g1,g3) = -1.5708
    c: Equal(g0,g1)
    c: Horizontal(g3)
    c: DistanceX(g0,g1) = 20
    c: Coincident(g10,g0)
    c: Coincident(g11,g1)
    c: Tangent(g4,g6) = 1.5708
    c: Tangent(g4,g7) = -1.5708
    c: Tangent(g5,g6) = 1.5708
    c: Tangent(g5,g7) = -1.5708
    c: Equal(g4,g5)
    c: Distance(g4,g5) = 2
    c: Radius(g4) = 2.7
    c: Coincident(g8,g4)
    c: Coincident(g9,g5)
    c: Coincident(g8,g9)
    c: Coincident(g10,g11)
    c: Coincident(g10,g8)
    c: Equal(g10,g11)
    c: Vertical(g8)
    c: Vertical(g9)
    c: Equal(g8,g9)
    c: Coincident(g8,g-1)
    c: Horizontal(g10)
    c: Radius(g1) = 7.7
FEATURE [PartDesign::Pad] Pad001  label="P-SlideBearing_Shaft"
  Direction = (0,0,1)
  Length = 2.3
  Length2 = 10
  Profile = -> Sketch012
  ReferenceAxis = -> Sketch012 [N_Axis]
  Refine = true
  Suppressed = false
  Type = 0
FEATURE [Sketcher::SketchObject] Sketch013  label="Sk-SlideBearing_Plate"
  ArcFitTolerance = 1e-06
  AttachmentSupport = -> [Pad001]
  ExternalGeometry = -> [Pad001]
  FullyConstrained = true
  MakeInternals = false
  MapMode = 5
  Placement = pos=(0,0,2.3) rot=(0,0,1;0rad)
  sketch-geometry (14):
    g0: ArcOfCircle CenterX=0 CenterY=1 CenterZ=0 NormalX=0 NormalY=0 NormalZ=1 AngleXU=0 Radius=2.7 StartAngle=2.524e-13 EndAngle=3.14159
    g1: ArcOfCircle CenterX=0 CenterY=-1 CenterZ=0 NormalX=0 NormalY=0 NormalZ=1 AngleXU=0 Radius=2.7 StartAngle=3.14159 EndAngle=6.28319
    g2: LineSegment StartX=2.7 StartY=1 StartZ=0 EndX=2.7 EndY=-1 EndZ=0
    g3: LineSegment StartX=-2.7 StartY=1 StartZ=0 EndX=-2.7 EndY=-1 EndZ=0
    g4: LineSegment StartX=-18.7 StartY=-17.7 StartZ=0 EndX=18.7 EndY=-17.7 EndZ=0
    g5: LineSegment StartX=18.7 StartY=-17.7 StartZ=0 EndX=18.7 EndY=17.7 EndZ=0
    g6: LineSegment StartX=18.7 StartY=17.7 StartZ=0 EndX=-18.7 EndY=17.7 EndZ=0
    g7: LineSegment StartX=-18.7 StartY=17.7 StartZ=0 EndX=-18.7 EndY=0 EndZ=0
    g8: LineSegment StartX=-18.7 StartY=0 StartZ=0 EndX=-18.7 EndY=-17.7 EndZ=0
    g9: LineSegment [constr] StartX=-10 StartY=7.7 StartZ=0 EndX=-10 EndY=17.7 EndZ=0
    g10: LineSegment [constr] StartX=-10 StartY=0 StartZ=0 EndX=-17.7 EndY=0 EndZ=0
    g11: LineSegment [constr] StartX=-17.7 StartY=0 StartZ=0 EndX=-18.7 EndY=0 EndZ=0
    g12: LineSegment [constr] StartX=10 StartY=2e-16 StartZ=0 EndX=17.7 EndY=2e-16 EndZ=0
    g13: LineSegment [constr] StartX=17.7 StartY=2e-16 StartZ=0 EndX=18.7 EndY=2e-16 EndZ=0
  constraints (38):
    c: Tangent(g0,g2) = 1.5708
    c: Tangent(g0,g3) = -1.5708
    c: Tangent(g1,g2) = 1.5708
    c: Tangent(g1,g3) = -1.5708
    c: Equal(g0,g1)
    c: Equal(g0,g-3)
    c: Coincident(g0,g-3)
    c: Coincident(g1,g-4)
    c: Vertical(g5)
    c: Horizontal(g4)
    c: Horizontal(g6)
    c: Coincident(g10,g-5)
    c: Coincident(g12,g-6)
    c: Coincident(g7,g8)
    c: Vertical(g7)
    c: Vertical(g8)
    c: Coincident(g7,g11)
    c: Equal(g7,g8)
    c: Coincident(g9,g-5)
    c: PointOnObject(g9,g6)
    c: Vertical(g9)
    c: DistanceY(g9,g9) = 10
    c: Coincident(g10,g11)
    c: Horizontal(g10)
    c: Horizontal(g11)
    c: PointOnObject(g10,g-5)
    c: DistanceX(g11,g11) = 1
    c: PointOnObject(g13,g5)
    c: Coincident(g12,g13)
    c: Horizontal(g12)
    c: Horizontal(g13)
    c: PointOnObject(g12,g-6)
    c: Equal(g11,g13)
    c: DistanceY(g13,g6) = 17.7
    c: Coincident(g7,g6)
    c: Coincident(g8,g4)
    c: Coincident(g5,g4)
    c: Coincident(g5,g6)
FEATURE [PartDesign::Pad] Pad002  label="P-SlideBearing_raw"
  BaseFeature = -> Pad001
  Direction = (0,0,1)
  Length = 4
  Length2 = 10
  Profile = -> Sketch013
  ReferenceAxis = -> Sketch013 [N_Axis]
  Refine = true
  Suppressed = false
  Type = 0
FEATURE [PartDesign::Chamfer] Chamfer  label="P-SlideBearing_Chamber"
  Angle = 45
  Base = -> Pad002 [Edge17,Edge18]
  BaseFeature = -> Pad002
  ChamferType = 0
  FlipDirection = false
  Refine = true
  Size = 1
  Size2 = 1
  SupportTransform = false
  Suppressed = false
  UseAllEdges = false
FEATURE [PartDesign::Fillet] Fillet  label="P-SlideBearing_rounded"
  Base = -> Chamfer [Edge9,Edge20,Edge18,Edge12]
  BaseFeature = -> Chamfer
  Radius = 1
  Refine = true
  SupportTransform = false
  Suppressed = false
  UseAllEdges = false
FEATURE [PartDesign::Body] Body003  label="B-Slide Bearing"
  AllowCompound = false
  Group = -> [Sketch012,Pad001,Sketch013,Pad002,Chamfer,Fillet]
  Origin = -> Origin005
  Placement = pos=(167.5,117,90) rot=(0,0,1;0rad)
  Tip = -> Fillet
FEATURE [Sketcher::SketchObject] Sketch014  label="Sk-Steppersledge-Switch_base001"
  ArcFitTolerance = 1e-06
  AttachmentSupport = -> [XY_Plane006]
  FullyConstrained = true
  MakeInternals = false
  MapMode = 5
  sketch-geometry (107):
    g0: Circle CenterX=379 CenterY=29 CenterZ=0 NormalX=0 NormalY=0 NormalZ=1 AngleXU=0 Radius=2.75
    g1: ArcOfCircle CenterX=28 CenterY=29 CenterZ=0 NormalX=0 NormalY=0 NormalZ=1 AngleXU=0 Radius=8 StartAngle=1.5708 EndAngle=4.71239
    g2: ArcOfCircle CenterX=319 CenterY=29 CenterZ=0 NormalX=0 NormalY=0 NormalZ=1 AngleXU=0 Radius=8 StartAngle=4.71239 EndAngle=7.85398
    g3: LineSegment StartX=28 StartY=37 StartZ=0 EndX=319 EndY=37 EndZ=0
    g4: LineSegment StartX=28 StartY=21 StartZ=0 EndX=319 EndY=21 EndZ=0
    g5: GeomPoint [constr] X=0 Y=58 Z=0
    g6: ArcOfCircle CenterX=5 CenterY=5 CenterZ=0 NormalX=0 NormalY=0 NormalZ=1 AngleXU=0 Radius=5 StartAngle=3.14159 EndAngle=4.71239
    g7: GeomPoint [constr] X=0 Y=0 Z=0
    g8: LineSegment StartX=485 StartY=48.6914 StartZ=0 EndX=485 EndY=53 EndZ=0
    g9: LineSegment StartX=485 StartY=5 StartZ=0 EndX=485 EndY=9.30863 EndZ=0
    g10: LineSegment [constr] StartX=485 StartY=9.30863 StartZ=0 EndX=485 EndY=48.6914 EndZ=0
    g11: ArcOfCircle CenterX=488.5 CenterY=29 CenterZ=0 NormalX=0 NormalY=0 NormalZ=1 AngleXU=0 Radius=20 StartAngle=1.7467 EndAngle=4.53648
    g12: LineSegment [constr] StartX=488.5 StartY=29 StartZ=0 EndX=485 EndY=29 EndZ=0
    g13: GeomPoint X=20 Y=29 Z=0
    g14: LineSegment StartX=-4e-16 StartY=56 StartZ=0 EndX=-4e-16 EndY=29 EndZ=0
    g15: LineSegment StartX=-4e-16 StartY=29 StartZ=0 EndX=-4e-16 EndY=5 EndZ=0
    g16: LineSegment [constr] StartX=460 StartY=58 StartZ=0 EndX=460 EndY=0 EndZ=0
    g17: LineSegment [constr] StartX=488.5 StartY=52.57 StartZ=0 EndX=464.93 EndY=52.57 EndZ=0
    g18: LineSegment [constr] StartX=488.5 StartY=5.43 StartZ=0 EndX=464.93 EndY=5.43 EndZ=0
    g19: LineSegment [constr] StartX=464.93 StartY=52.57 StartZ=0 EndX=464.93 EndY=5.43 EndZ=0
    g20: LineSegment [constr] StartX=488.5 StartY=52.57 StartZ=0 EndX=488.5 EndY=29 EndZ=0
    g21: LineSegment [constr] StartX=488.5 StartY=29 StartZ=0 EndX=488.5 EndY=5.43 EndZ=0
    g22: ArcOfCircle CenterX=480 CenterY=53 CenterZ=0 NormalX=0 NormalY=0 NormalZ=1 AngleXU=0 Radius=5 StartAngle=0 EndAngle=1.5708
    g23: GeomPoint [constr] X=485 Y=58 Z=0
    g24: ArcOfCircle CenterX=480 CenterY=5 CenterZ=0 NormalX=0 NormalY=0 NormalZ=1 AngleXU=0 Radius=5 StartAngle=4.71239 EndAngle=6.28319
    g25: GeomPoint [constr] X=485 Y=0 Z=0
    g26: Circle CenterX=464.93 CenterY=52.57 CenterZ=0 NormalX=0 NormalY=0 NormalZ=1 AngleXU=0 Radius=2.6
    g27: Circle CenterX=464.93 CenterY=5.43 CenterZ=0 NormalX=0 NormalY=0 NormalZ=1 AngleXU=0 Radius=2.6
    g28: LineSegment [constr] StartX=460.83 StartY=50.2029 StartZ=0 EndX=464.93 EndY=47.8357 EndZ=0
    g29: LineSegment [constr] StartX=464.93 StartY=47.8357 StartZ=0 EndX=469.03 EndY=50.2029 EndZ=0
    g30: LineSegment [constr] StartX=469.03 StartY=50.2029 StartZ=0 EndX=469.03 EndY=54.9371 EndZ=0
    g31: LineSegment [constr] StartX=469.03 StartY=54.9371 StartZ=0 EndX=464.93 EndY=57.3043 EndZ=0
    g32: LineSegment [constr] StartX=464.93 StartY=57.3043 StartZ=0 EndX=460.83 EndY=54.9371 EndZ=0
    g33: LineSegment [constr] StartX=460.83 StartY=54.9371 StartZ=0 EndX=460.83 EndY=50.2029 EndZ=0
    g34: Circle [constr] CenterX=464.93 CenterY=52.57 CenterZ=0 NormalX=0 NormalY=0 NormalZ=1 AngleXU=0 Radius=4.73427
    g35: LineSegment StartX=458 StartY=58 StartZ=0 EndX=400 EndY=58 EndZ=0
    g36: LineSegment StartX=480 StartY=58 StartZ=0 EndX=462 EndY=58 EndZ=0
    g37: LineSegment [constr] StartX=462 StartY=58 StartZ=0 EndX=458 EndY=58 EndZ=0
    g38: ArcOfCircle CenterX=460 CenterY=58 CenterZ=0 NormalX=0 NormalY=0 NormalZ=1 AngleXU=0 Radius=2 StartAngle=3.14159 EndAngle=6.28319
    g39: LineSegment StartX=462 StartY=0 StartZ=0 EndX=480 EndY=0 EndZ=0
    g40: LineSegment [constr] StartX=5 StartY=0 StartZ=0 EndX=458 EndY=0 EndZ=0
    g41: LineSegment [constr] StartX=458 StartY=0 StartZ=0 EndX=462 EndY=0 EndZ=0
    g42: ArcOfCircle CenterX=460 CenterY=0 CenterZ=0 NormalX=0 NormalY=0 NormalZ=1 AngleXU=0 Radius=2 StartAngle=0 EndAngle=3.14159
    g43: LineSegment StartX=15 StartY=-10 StartZ=0 EndX=448 EndY=-10 EndZ=0
    g44: LineSegment StartX=448 StartY=-10 StartZ=0 EndX=458 EndY=0 EndZ=0
    g45: LineSegment StartX=15 StartY=-10 StartZ=0 EndX=5 EndY=0 EndZ=0
    g46: LineSegment [constr] StartX=-4e-16 StartY=56 StartZ=0 EndX=-4e-16 EndY=60 EndZ=0
    g47: LineSegment StartX=5 StartY=112 StartZ=0 EndX=342 EndY=112 EndZ=0
    g48: ArcOfCircle CenterX=5 CenterY=107 CenterZ=0 NormalX=0 NormalY=0 NormalZ=1 AngleXU=0 Radius=5 StartAngle=1.5708 EndAngle=3.14159
    g49: GeomPoint [constr] X=0 Y=112 Z=0
    g50: ArcOfCircle CenterX=342 CenterY=107 CenterZ=0 NormalX=0 NormalY=0 NormalZ=1 AngleXU=0 Radius=5 StartAngle=8e-16 EndAngle=1.5708
    g51: GeomPoint [constr] X=347 Y=112 Z=0
    g52: LineSegment StartX=400 StartY=58 StartZ=0 EndX=349 EndY=58 EndZ=0
    g53: LineSegment [constr] StartX=349 StartY=58 StartZ=0 EndX=347 EndY=58 EndZ=0
    g54: ArcOfCircle CenterX=0 CenterY=58 CenterZ=0 NormalX=0 NormalY=0 NormalZ=1 AngleXU=0 Radius=2 StartAngle=4.71239 EndAngle=7.85398
    g55: LineSegment [constr] StartX=347 StartY=60 StartZ=0 EndX=347 EndY=58 EndZ=0
    g56: GeomPoint [constr] X=327 Y=29 Z=0
    g57: LineSegment [constr] StartX=327 StartY=29 StartZ=0 EndX=347 EndY=29 EndZ=0
    g58: LineSegment [constr] StartX=347 StartY=29 StartZ=0 EndX=347 EndY=58 EndZ=0
    g59: LineSegment [constr] StartX=-4e-16 StartY=29 StartZ=0 EndX=20 EndY=29 EndZ=0
    g60: LineSegment [constr] StartX=485 StartY=29 StartZ=0 EndX=460 EndY=29 EndZ=0
    g61: LineSegment [constr] StartX=460 StartY=29 StartZ=0 EndX=400 EndY=29 EndZ=0
    g62: LineSegment [constr] StartX=400 StartY=29 StartZ=0 EndX=379 EndY=29 EndZ=0
    g63: LineSegment [constr] StartX=379 StartY=29 StartZ=0 EndX=347 EndY=29 EndZ=0
    g64: LineSegment [constr] StartX=327 StartY=29 StartZ=0 EndX=20 EndY=29 EndZ=0
    g65: LineSegment [constr] StartX=400 StartY=58 StartZ=0 EndX=400 EndY=29 EndZ=0
    g66: LineSegment [constr] StartX=400 StartY=29 StartZ=0 EndX=400 EndY=0 EndZ=0
    g67: LineSegment [constr] StartX=0 StartY=58 StartZ=0 EndX=347 EndY=58 EndZ=0
    g68: ArcOfCircle CenterX=347 CenterY=58 CenterZ=0 NormalX=0 NormalY=0 NormalZ=1 AngleXU=0 Radius=2 StartAngle=1.5708 EndAngle=6.28319
    g69: LineSegment [constr] StartX=28 StartY=29 StartZ=0 EndX=28 EndY=58 EndZ=0
    g70: LineSegment [constr] StartX=28 StartY=58 StartZ=0 EndX=28 EndY=78 EndZ=0
    g71: LineSegment [constr] StartX=28 StartY=78 StartZ=0 EndX=28 EndY=88 EndZ=0
    g72: LineSegment [constr] StartX=28 StartY=88 StartZ=0 EndX=28 EndY=95 EndZ=0
    g73: LineSegment StartX=-4e-16 StartY=60 StartZ=0 EndX=-4e-16 EndY=86 EndZ=0
    g74: LineSegment [constr] StartX=-4e-16 StartY=86 StartZ=0 EndX=-4e-16 EndY=90 EndZ=0
    g75: LineSegment StartX=-4e-16 StartY=90 StartZ=0 EndX=-4e-16 EndY=93 EndZ=0
    g76: LineSegment [constr] StartX=-4e-16 StartY=93 StartZ=0 EndX=-4e-16 EndY=97 EndZ=0
    g77: LineSegment StartX=-4e-16 StartY=97 StartZ=0 EndX=-4e-16 EndY=107 EndZ=0
    g78: LineSegment StartX=347 StartY=107 StartZ=0 EndX=347 EndY=97 EndZ=0
    g79: LineSegment [constr] StartX=347 StartY=97 StartZ=0 EndX=347 EndY=93 EndZ=0
    g80: LineSegment StartX=347 StartY=93 StartZ=0 EndX=347 EndY=90 EndZ=0
    g81: LineSegment [constr] StartX=347 StartY=90 StartZ=0 EndX=347 EndY=86 EndZ=0
    g82: LineSegment StartX=347 StartY=86 StartZ=0 EndX=347 EndY=60 EndZ=0
    g83: LineSegment [constr] StartX=0 StartY=88 StartZ=0 EndX=347 EndY=88 EndZ=0
    g84: LineSegment [constr] StartX=347 StartY=95 StartZ=0 EndX=0 EndY=95 EndZ=0
    g85: ArcOfCircle CenterX=0 CenterY=88 CenterZ=0 NormalX=0 NormalY=0 NormalZ=1 AngleXU=0 Radius=2 StartAngle=4.71239 EndAngle=7.85398
    g86: ArcOfCircle CenterX=0 CenterY=95 CenterZ=0 NormalX=0 NormalY=0 NormalZ=1 AngleXU=0 Radius=2 StartAngle=4.71239 EndAngle=7.85398
    g87: ArcOfCircle CenterX=347 CenterY=95 CenterZ=0 NormalX=0 NormalY=0 NormalZ=1 AngleXU=0 Radius=2 StartAngle=1.5708 EndAngle=4.71239
    g88: ArcOfCircle CenterX=347 CenterY=88 CenterZ=0 NormalX=0 NormalY=0 NormalZ=1 AngleXU=0 Radius=2 StartAngle=1.5708 EndAngle=4.71239
    g89: LineSegment [constr] StartX=0 StartY=78 StartZ=0 EndX=347 EndY=78 EndZ=0
    g90: LineSegment [constr] StartX=28 StartY=95 StartZ=0 EndX=28 EndY=105 EndZ=0
    g91: LineSegment [constr] StartX=28 StartY=105 StartZ=0 EndX=28 EndY=112 EndZ=0
    g92: LineSegment [constr] StartX=0 StartY=105 StartZ=0 EndX=347 EndY=105 EndZ=0
    g93: ArcOfCircle CenterX=21.5006 CenterY=78 CenterZ=0 NormalX=0 NormalY=0 NormalZ=1 AngleXU=0 Radius=1.5 StartAngle=1.5708 EndAngle=4.71239
    g94: ArcOfCircle CenterX=325.5 CenterY=78 CenterZ=0 NormalX=0 NormalY=0 NormalZ=1 AngleXU=0 Radius=1.5 StartAngle=4.71239 EndAngle=7.85398
    g95: LineSegment StartX=21.5006 StartY=79.5 StartZ=0 EndX=325.5 EndY=79.5 EndZ=0
    g96: LineSegment StartX=21.5006 StartY=76.5 StartZ=0 EndX=325.5 EndY=76.5 EndZ=0
    g97: ArcOfCircle CenterX=21.5006 CenterY=105 CenterZ=0 NormalX=0 NormalY=0 NormalZ=1 AngleXU=0 Radius=1.5 StartAngle=1.5708 EndAngle=4.71239
    g98: ArcOfCircle CenterX=325.5 CenterY=105 CenterZ=0 NormalX=0 NormalY=0 NormalZ=1 AngleXU=0 Radius=1.5 StartAngle=4.71239 EndAngle=7.85398
    g99: LineSegment StartX=21.5006 StartY=106.5 StartZ=0 EndX=325.5 EndY=106.5 EndZ=0
    g100: LineSegment StartX=21.5006 StartY=103.5 StartZ=0 EndX=325.5 EndY=103.5 EndZ=0
    g101: GeomPoint X=327 Y=78 Z=0
    g102: GeomPoint X=20.0006 Y=78 Z=0
    g103: LineSegment [constr] StartX=21.5006 StartY=105 StartZ=0 EndX=21.5006 EndY=78 EndZ=0
    g104: LineSegment [constr] StartX=20.0006 StartY=78 StartZ=0 EndX=20 EndY=29 EndZ=0
    g105: LineSegment [constr] StartX=325.5 StartY=105 StartZ=0 EndX=325.5 EndY=78 EndZ=0
    g106: LineSegment [constr] StartX=327 StartY=78 StartZ=0 EndX=327 EndY=29 EndZ=0
  constraints (278):
    c: Diameter(g0) = 5.5
    c: Tangent(g1,g3) = 1.5708
    c: Tangent(g1,g4) = -1.5708
    c: Tangent(g2,g3) = 1.5708
    c: Tangent(g2,g4) = -1.5708
    c: Equal(g1,g2)
    c: Horizontal(g4)
    c: Coincident(g35,g52)
    c: DistanceY(g66,g65) = 58
    c: Coincident(g35,g65)
    c: Coincident(g10,g8)
    c: Vertical(g8)
    c: Coincident(g9,g10)
    c: Vertical(g9)
    c: Vertical(g10)
    c: Coincident(g11,g8)
    c: Coincident(g11,g9)
    c: Coincident(g12,g11)
    c: Horizontal(g12)
    c: Radius(g11) = 20
    c: DistanceX(g12,g12) = 3.5
    c: DistanceX(g15,g66) = 400
    c: Coincident(g14,g15)
    c: PointOnObject(g7,g14)
    c: DistanceX(g14,g13) = 20
    c: Vertical(g14)
    c: Tangent(g15,g6) = -1.5708
    c: Vertical(g15)
    c: DistanceX(g0,g66) = 21
    c: DistanceX(g2,g0) = 60
    c: Vertical(g16)
    c: DistanceX(g66,g16) = 60
    c: Coincident(g17,g20)
    c: Horizontal(g17)
    c: Coincident(g18,g21)
    c: Horizontal(g18)
    c: Coincident(g19,g17)
    c: Coincident(g19,g18)
    c: Vertical(g19)
    c: Coincident(g20,g21)
    c: Vertical(g20)
    c: Vertical(g21)
    c: Equal(g20,g21)
    c: DistanceY(g18,g17) = 47.14
    c: Equal(g20,g17)
    c: PointOnObject(g23,g8)
    c: Tangent(g8,g22) = -1.5708
    c: PointOnObject(g25,g9)
    c: Tangent(g9,g24) = -1.5708
    c: Equal(g24,g22)
    c: DistanceX(g16,g18) = 28.5
    c: Coincident(g26,g17)
    c: Diameter(g26) = 5.2
    c: Coincident(g27,g18)
    c: Equal(g26,g27)
    c: Coincident(g28,g29)
    c: Coincident(g29,g30)
    c: Coincident(g30,g31)
    c: Coincident(g31,g32)
    c: Coincident(g32,g33)
    c: Coincident(g33,g28)
    c: Equal(g28, g29-g33) x5
    c: PointOnObject(g28,g34)
    c: PointOnObject(g29,g34)
    c: PointOnObject(g30,g34)
    c: PointOnObject(g31,g34)
    c: PointOnObject(g32,g34)
    c: PointOnObject(g33,g34)
    c: Coincident(g34,g17)
    c: Vertical(g33)
    c: DistanceX(g32,g30) = 8.2
    c: Radius(g2) = 8
    c: Coincident(g37,g35)
    c: Horizontal(g35)
    c: Coincident(g36,g37)
    c: Horizontal(g36)
    c: Horizontal(g37)
    c: PointOnObject(g16,g36)
    c: PointOnObject(g23,g36)
    c: Coincident(g38,g16)
    c: Coincident(g38,g35)
    c: Coincident(g38,g36)
    c: Radius(g38) = 2
    c: Tangent(g36,g22) = -1.5708
    c: Coincident(g41,g39)
    c: Horizontal(g39)
    c: PointOnObject(g66,g39)
    c: PointOnObject(g16,g39)
    c: PointOnObject(g25,g39)
    c: Coincident(g40,g41)
    c: Horizontal(g40)
    c: Horizontal(g41)
    c: PointOnObject(g7,g40)
    c: Coincident(g42,g16)
    c: Coincident(g42,g39)
    c: Coincident(g42,g40)
    c: Tangent(g39,g24) = -1.5708
    c: Equal(g42,g38)
    c: Tangent(g40,g6) = -1.5708
    c: Horizontal(g43)
    c: Coincident(g43,g44)
    c: Coincident(g44,g40)
    c: Coincident(g45,g43)
    c: Coincident(g45,g6)
    c: Angle(g45,g40) = 0.785398
    c: Equal(g45,g44)
    c: DistanceY(g43,g6) = 10
    c: Vertical(g46)
    c: Coincident(g46,g73)
    c: Horizontal(g47)
    c: Radius(g6) = 5
    c: PointOnObject(g49,g47)
    c: Tangent(g47,g48) = 1.5708
    c: PointOnObject(g51,g47)
    c: Tangent(g47,g50) = 1.5708
    c: Coincident(g52,g53)
    c: Horizontal(g52)
    c: Horizontal(g53)
    c: Equal(g6,g48)
    c: Equal(g48,g50)
    c: Coincident(g14,g46)
    c: Coincident(g54,g5)
    c: Coincident(g54,g14)
    c: Coincident(g54,g46)
    c: Coincident(g57,g56)
    c: Coincident(g58,g57)
    c: Vertical(g58)
    c: Coincident(g59,g14)
    c: Coincident(g59,g13)
    c: Equal(g59,g57)
    c: PointOnObject(g5,g46)
    c: Horizontal(g57)
    c: Coincident(g11,g20)
    c: Coincident(g60,g12)
    c: PointOnObject(g60,g16)
    c: Horizontal(g60)
    c: Coincident(g61,g60)
    c: Horizontal(g61)
    c: Coincident(g62,g61)
    c: Coincident(g62,g0)
    c: Coincident(g63,g0)
    c: Coincident(g63,g57)
    c: Horizontal(g63)
    c: Horizontal(g62)
    c: Coincident(g64,g56)
    c: PointOnObject(g64,g1)
    c: Horizontal(g64)
    c: Coincident(g13,g64)
    c: PointOnObject(g1,g64)
    c: Horizontal(g59)
    c: PointOnObject(g56,g2)
    c: PointOnObject(g12,g10)
    c: Coincident(g65,g66)
    c: Vertical(g65)
    c: Vertical(g66)
    c: Coincident(g65,g61)
    c: Equal(g65,g66)
    c: Equal(g24,g6)
    c: Coincident(g67,g5)
    c: Horizontal(g67)
    c: Vertical(g55)
    c: Coincident(g58,g55)
    c: Coincident(g53,g55)
    c: Coincident(g82,g55)
    c: Coincident(g67,g53)
    c: Coincident(g68,g53)
    c: Coincident(g68,g55)
    c: Coincident(g68,g52)
    c: Equal(g54,g68)
    c: Equal(g68,g38)
    c: Coincident(g7,g-1)
    c: Coincident(g69,g1)
    c: PointOnObject(g69,g67)
    c: Vertical(g69)
    c: Coincident(g70,g69)
    c: Vertical(g70)
    c: Coincident(g71,g70)
    c: Vertical(g71)
    c: Coincident(g72,g71)
    c: PointOnObject(g91,g47)
    c: DistanceY(g70,g70) = 20
    c: DistanceY(g71,g71) = 10
    c: Coincident(g72,g90)
    c: Vertical(g72)
    c: DistanceY(g72,g72) = 7
    c: Coincident(g73,g74)
    c: Vertical(g73)
    c: PointOnObject(g49,g73)
    c: Coincident(g74,g75)
    c: Vertical(g74)
    c: Coincident(g75,g76)
    c: Vertical(g75)
    c: Coincident(g76,g77)
    c: Vertical(g76)
    c: Vertical(g77)
    c: Tangent(g77,g48) = 1.5708
    c: Coincident(g78,g79)
    c: Vertical(g78)
    c: PointOnObject(g51,g78)
    c: Coincident(g79,g80)
    c: Vertical(g79)
    c: Coincident(g80,g81)
    c: Vertical(g80)
    c: Coincident(g81,g82)
    c: Vertical(g81)
    c: Vertical(g82)
    c: Tangent(g78,g50) = 1.5708
    c: PointOnObject(g83,g74)
    c: PointOnObject(g83,g81)
    c: Horizontal(g83)
    c: PointOnObject(g84,g79)
    c: PointOnObject(g84,g76)
    c: Horizontal(g84)
    c: Coincident(g85,g83)
    c: Coincident(g85,g74)
    c: Coincident(g85,g73)
    c: Coincident(g86,g84)
    c: Coincident(g86,g76)
    c: Coincident(g86,g75)
    c: Coincident(g87,g84)
    c: Coincident(g87,g78)
    c: Coincident(g87,g79)
    c: Coincident(g88,g83)
    c: Coincident(g88,g80)
    c: Coincident(g88,g81)
    c: Equal(g54,g85)
    c: Equal(g85,g86)
    c: Equal(g86,g87)
    c: Equal(g87,g88)
    c: PointOnObject(g72,g84)
    c: PointOnObject(g71,g83)
    c: PointOnObject(g89,g73)
    c: PointOnObject(g89,g82)
    c: Horizontal(g89)
    c: PointOnObject(g70,g89)
    c: Coincident(g90,g91)
    c: Vertical(g90)
    c: Vertical(g91)
    c: Equal(g71,g90)
    c: DistanceY(g91,g91) = 7
    c: PointOnObject(g92,g77)
    c: PointOnObject(g92,g78)
    c: Horizontal(g92)
    c: PointOnObject(g90,g92)
    c: Tangent(g93,g95) = 1.5708
    c: Tangent(g93,g96) = -1.5708
    c: Tangent(g94,g95) = 1.5708
    c: Tangent(g94,g96) = -1.5708
    c: Equal(g93,g94)
    c: Horizontal(g96)
    c: Radius(g93) = 1.5
    c: PointOnObject(g93,g89)
    c: Tangent(g97,g99) = 1.5708
    c: Tangent(g97,g100) = -1.5708
    c: Tangent(g98,g99) = 1.5708
    c: Tangent(g98,g100) = -1.5708
    c: Equal(g97,g98)
    c: Horizontal(g100)
    c: PointOnObject(g97,g92)
    c: Equal(g98,g94)
    c: PointOnObject(g101,g89)
    c: PointOnObject(g101,g94)
    c: PointOnObject(g102,g89)
    c: PointOnObject(g102,g93)
    c: Coincident(g103,g97)
    c: Coincident(g103,g93)
    c: Vertical(g103)
    c: Coincident(g104,g102)
    c: Coincident(g104,g13)
    c: Tangent(g104,g93)
    c: Coincident(g105,g98)
    c: Coincident(g105,g94)
    c: Coincident(g106,g101)
    c: Coincident(g106,g56)
    c: Vertical(g106)
    c: Vertical(g105)
    c: DistanceY(g90,g90) = 10
    c: DistanceX(g57,g57) = 20
FEATURE [PartDesign::FeaturePython] BaseBend002  label="S-Steppersledge-Switch_base001"  # WARN: FeaturePython — macro-defined, semantics opaque (R4)
  BendSide = 0
  BendSketch = -> Sketch014
  Length = 100
  MidPlane = false
  Radius = 2
  Reverse = false
  Suppressed = false
  Thickness = 1
FEATURE [Sketcher::SketchObject] Sketch015  label="Sk-SsSw_Bendline_Steppermount001"
  ArcFitTolerance = 1e-06
  AttachmentSupport = -> [BaseBend002]
  ExternalGeometry = -> [BaseBend002]
  FullyConstrained = true
  MakeInternals = false
  MapMode = 5
  Placement = pos=(0,0,0) rot=(1,0,0;3.14159rad)
  sketch-geometry (1):
    g0: LineSegment StartX=460 StartY=-58 StartZ=0 EndX=460 EndY=0 EndZ=0
  constraints (2):
    c: Coincident(g0,g-4)
    c: Coincident(g-3,g0)
FEATURE [PartDesign::FeaturePython] Fold008  label="Fd-Steppersledge-Sw-Mount001"  # WARN: FeaturePython — macro-defined, semantics opaque (R4)
  BaseFeature = -> BaseBend002
  BendLine = -> Sketch015
  Position = 1
  Suppressed = false
  angle = 90
  baseObject = -> BaseBend002 [Face48]
  invert = false
  invertbend = false
  kfactor = 0.5
  radius = 2
  unfold = false
FEATURE [Sketcher::SketchObject] Sketch016  label="Sk-SsSw_Bendline-Seam-Bottom001"
  ArcFitTolerance = 1e-06
  AttachmentSupport = -> [Fold008]
  ExternalGeometry = -> [Fold008]
  FullyConstrained = true
  MakeInternals = false
  MapMode = 5
  Placement = pos=(0,0,0) rot=(1,0,0;3.14159rad)
  sketch-geometry (2):
    g0: LineSegment StartX=0 StartY=0 StartZ=0 EndX=460.037 EndY=0 EndZ=0
    g1: LineSegment [constr] StartX=0 StartY=0 StartZ=0 EndX=0 EndY=-5 EndZ=0
  constraints (5):
    c: Horizontal(g0)
    c: Coincident(g1,g0)
    c: Coincident(g1,g-3)
    c: Vertical(g1)
    c: Coincident(g0,g-4)
FEATURE [PartDesign::FeaturePython] Fold009  label="Fd-Steppersledge-Sw-Seam001"  # WARN: FeaturePython — macro-defined, semantics opaque (R4)
  BaseFeature = -> Fold008
  BendLine = -> Sketch016
  Position = 1
  Suppressed = false
  angle = 182
  baseObject = -> Fold008 [Face3]
  invert = false
  invertbend = false
  kfactor = 0.5
  radius = 0.2
  unfold = false
FEATURE [Sketcher::SketchObject] Sketch017  label="Sk-SsSw_Bendline-Switchprofile_004"
  ArcFitTolerance = 1e-06
  AttachmentSupport = -> [Fold009]
  FullyConstrained = true
  MakeInternals = false
  MapMode = 5
  Placement = pos=(0,0,1) rot=(0,0,1;0rad)
  sketch-geometry (1):
    g0: LineSegment StartX=0 StartY=95 StartZ=0 EndX=347 EndY=95 EndZ=0
  constraints (2):
    c: Coincident(g0,g-3)
    c: Coincident(g0,g-4)
FEATURE [PartDesign::FeaturePython] Fold010  label="Fd-Steppersledge-Sw-Profile-btm001"  # WARN: FeaturePython — macro-defined, semantics opaque (R4)
  BaseFeature = -> Fold009
  BendLine = -> Sketch017
  Position = 1
  Suppressed = false
  angle = 90
  baseObject = -> Fold009 [Face50]
  invert = false
  invertbend = false
  kfactor = 0.5
  radius = 2
  unfold = false
FEATURE [Sketcher::SketchObject] Sketch018  label="Sk-SsSw_Bendline-Switchprofile_005"
  ArcFitTolerance = 1e-06
  AttachmentSupport = -> [Fold010]
  FullyConstrained = true
  MakeInternals = false
  MapMode = 5
  Placement = pos=(0,0,1) rot=(0,0,1;0rad)
  sketch-geometry (1):
    g0: LineSegment StartX=0 StartY=88 StartZ=0 EndX=347 EndY=88 EndZ=0
  constraints (2):
    c: Coincident(g0,g-3)
    c: Coincident(g0,g-4)
FEATURE [PartDesign::FeaturePython] Fold011  label="Fd-Steppersledge-Sw-Profile-outer001"  # WARN: FeaturePython — macro-defined, semantics opaque (R4)
  BaseFeature = -> Fold010
  BendLine = -> Sketch018
  Position = 1
  Suppressed = false
  angle = 90
  baseObject = -> Fold010 [Face2]
  invert = false
  invertbend = false
  kfactor = 0.5
  radius = 2
  unfold = false
FEATURE [Sketcher::SketchObject] Sketch019  label="Sk-SsSw_Bendline-Switchprofile_006"
  ArcFitTolerance = 1e-06
  AttachmentSupport = -> [Fold011]
  FullyConstrained = true
  MakeInternals = false
  MapMode = 5
  Placement = pos=(0,87.9635,0) rot=(0,0.707107,0.707107;3.14159rad)
  sketch-geometry (1):
    g0: LineSegment StartX=-347 StartY=31 StartZ=0 EndX=0 EndY=31 EndZ=0
  constraints (2):
    c: Coincident(g0,g-3)
    c: Coincident(g0,g-4)
FEATURE [PartDesign::FeaturePython] Fold012  label="Fd-Steppersledge-Sw-complete001"  # WARN: FeaturePython — macro-defined, semantics opaque (R4)
  BaseFeature = -> Fold011
  BendLine = -> Sketch019
  Position = 1
  Suppressed = false
  angle = 90
  baseObject = -> Fold011 [Face2]
  invert = false
  invertbend = false
  kfactor = 0.5
  radius = 2
  unfold = false
FEATURE [PartDesign::Body] Body004  label="B-Steppersledge Switch-U-Profile"
  AllowCompound = false
  Group = -> [Sketch014,BaseBend002,Fold008,Fold009,Fold010,Fold011,Fold012]
  Origin = -> Origin006
  Tip = -> Fold012
FEATURE [PartDesign::FeaturePython] Fold013  label="Fd-Steppersledge-Sw-complete"  # WARN: FeaturePython — macro-defined, semantics opaque (R4)
  BaseFeature = -> Fold001
  BendLine = -> Sketch006
  Position = 1
  Suppressed = false
  angle = 90
  baseObject = -> Fold001 [?Face38]
  invert = false
  invertbend = false
  kfactor = 0.5
  radius = 2
  unfold = false
FEATURE [PartDesign::Body] Body  label="B-Steppersledge Switch"
  AllowCompound = false
  Group = -> [Sketch,BaseBend,Fold,Fold001,Fold013]
  Origin = -> Origin
  Placement = pos=(0,146,29.4) rot=(1,0,0;3.14159rad)
  Tip = -> Fold013
FEATURE [Part::FeaturePython] Body_Unfold  label="B-Steppersledge Switch_Unfold"  # WARN: FeaturePython — macro-defined, semantics opaque (R4)
  GenerateSketch = false
  KFactor = 0.4
  KFactorStandard = 0
  ManualRecompute = false
  MaterialSheet = _manual
  SeparateSketchLayers = true
  baseObject = -> Fold013 [Face69]
FEATURE [TechDraw::DrawProjGroupItem] View  label="Stepper Mount - plain CNC"
  CoarseView = false
  Direction = (-1,-1e-16,0)
  Focus = 100
  HardHidden = true
  IsoCount = 0
  IsoHidden = false
  IsoVisible = false
  LockPosition = true
  Perspective = false
  Rotation = 0
  RotationVector = (1,0,0)
  Scale = 0.5
  ScaleType = 2
  ScrubCount = 3
  SeamHidden = false
  SeamVisible = false
  SmoothHidden = true
  SmoothVisible = true
  Source = -> [Body001_Unfold]
  Type = 0
  X = 147.655
  XDirection = (0,-1e-16,-1)
  Y = 157.316
FEATURE [TechDraw::DrawProjGroupItem] View001  label="Stepper Mount - Switches CNC"
  CoarseView = false
  Direction = (1,1e-16,0)
  Focus = 100
  HardHidden = true
  IsoCount = 0
  IsoHidden = false
  IsoVisible = false
  LockPosition = true
  Perspective = false
  Rotation = 0
  RotationVector = (1,0,0)
  Scale = 0.5
  ScaleType = 2
  ScrubCount = 1
  SeamHidden = false
  SeamVisible = false
  SmoothHidden = false
  SmoothVisible = true
  Source = -> [Body_Unfold]
  Type = 0
  X = 147.655
  XDirection = (0,-3e-16,-1)
  Y = 87.6941
FEATURE [TechDraw::DrawPage] Page001  label="Mover Stepper Mounts - CNC Template"
  KeepUpdated = true
  NextBalloonIndex = 1
  ProjectionType = 0
  Template = -> Template001
  Views = -> [View,View001]
FEATURE [TechDraw::DrawSVGTemplate] Template  label="Vorlage"
  EditableTexts = AUTHOR_NAME=Unseen Obstacles; DN=02; DRAWING_TITLE=Mover Stepper Mounts; FC-DATE=20/10/2025; FC-REV=r 01.10; FC-SC=1 : 2; FC-SH=1 / 1; FC-SI=A4; FreeCAD_DRAWING=Bend Radius: 2 mm; PN=01; SI-1=Material: 2 mm Steel Sheet
  Height = 210
  Orientation = 1
  Template = <path>
  Width = 297
FEATURE [TechDraw::DrawProjGroupItem] View002  label="Stepper Mount - plain"
  CoarseView = false
  Direction = (-1,-1e-16,0)
  Focus = 100
  HardHidden = true
  IsoCount = 0
  IsoHidden = false
  IsoVisible = false
  LockPosition = true
  Perspective = false
  Rotation = 0
  RotationVector = (1,0,0)
  Scale = 0.5
  ScaleType = 2
  ScrubCount = 1
  SeamHidden = false
  SeamVisible = false
  SmoothHidden = false
  SmoothVisible = true
  Source = -> [Body001_Unfold]
  Type = 0
  X = 148.079
  XDirection = (0,2e-16,-1)
  Y = 157.212
FEATURE [TechDraw::DrawProjGroupItem] View003  label="Stepper Mount - Switches"
  CoarseView = false
  Direction = (1,0,-1e-16)
  Focus = 100
  HardHidden = true
  IsoCount = 0
  IsoHidden = false
  IsoVisible = false
  LockPosition = true
  Perspective = false
  Rotation = 0
  RotationVector = (1,0,0)
  Scale = 0.5
  ScaleType = 2
  ScrubCount = 1
  SeamHidden = false
  SeamVisible = false
  SmoothHidden = false
  SmoothVisible = true
  Source = -> [Body_Unfold]
  Type = 0
  X = 148.079
  XDirection = (-1e-16,-1e-16,-1)
  Y = 87.6941
FEATURE [TechDraw::DrawViewDimension] Dimension001  label="Maß001"
  AngleOverride = false
  Arbitrary = false
  ArbitraryTolerances = false
  BoxCorners = (2) [(-121.671,-22.6841,0),(121.671,22.6841,0)]
  EqualTolerance = true
  ExtensionAngle = 0
  FormatSpec = R%.1w
  FormatSpecOverTolerance = %+.1w
  FormatSpecUnderTolerance = %+.1w
  Inverted = false
  LineAngle = 0
  LockPosition = false
  MeasureType = 1
  OverTolerance = 0
  References2D = -> [View002]
  Rotation = 0
  ScaleType = 0
  TheoreticalExact = false
  Type = 4
  UnderTolerance = 0
  X = 126.622
  Y = 12.0098
FEATURE [TechDraw::DrawViewDimension] Dimension002  label="Maß002"
  AngleOverride = false
  Arbitrary = false
  ArbitraryTolerances = false
  BoxCorners = (2) [(-121.671,-22.6841,0),(121.671,22.6841,0)]
  EqualTolerance = true
  ExtensionAngle = 0
  FormatSpec = R%.1w
  FormatSpecOverTolerance = %+.1w
  FormatSpecUnderTolerance = %+.1w
  Inverted = false
  LineAngle = 0
  LockPosition = false
  MeasureType = 1
  OverTolerance = 0
  References2D = -> [View002]
  Rotation = 0
  ScaleType = 0
  TheoreticalExact = false
  Type = 4
  UnderTolerance = 0
  X = -108.238
  Y = 13.276
FEATURE [TechDraw::DrawViewDimension] Dimension003  label="Maß003"
  AngleOverride = false
  Arbitrary = false
  ArbitraryTolerances = false
  BoxCorners = (2) [(-121.671,-22.6841,0),(121.671,22.6841,0)]
  EqualTolerance = true
  ExtensionAngle = 0
  FormatSpec = R%.1w
  FormatSpecOverTolerance = %+.1w
  FormatSpecUnderTolerance = %+.1w
  Inverted = false
  LineAngle = 0
  LockPosition = false
  MeasureType = 1
  OverTolerance = 0
  References2D = -> [View002]
  Rotation = 0
  ScaleType = 0
  TheoreticalExact = false
  Type = 4
  UnderTolerance = 0
  X = 43.4536
  Y = 12.6249
FEATURE [TechDraw::DrawViewDimension] Dimension004  label="Maß004"
  AngleOverride = false
  Arbitrary = false
  ArbitraryTolerances = false
  BoxCorners = (2) [(-121.671,-22.6841,0),(121.671,22.6841,0)]
  EqualTolerance = true
  ExtensionAngle = 0
  FormatSpec = ⌀%.1w
  FormatSpecOverTolerance = %+.1w
  FormatSpecUnderTolerance = %+.1w
  Inverted = false
  LineAngle = 0
  LockPosition = false
  MeasureType = 1
  OverTolerance = 0
  References2D = -> [View002]
  Rotation = 0
  ScaleType = 0
  TheoreticalExact = false
  Type = 5
  UnderTolerance = 0
  X = 70.1626
  Y = 12.484
FEATURE [TechDraw::DrawViewDimension] Dimension005  label="Maß005"
  AngleOverride = false
  Arbitrary = false
  ArbitraryTolerances = false
  BoxCorners = (2) [(-121.671,-22.6841,0),(121.671,22.6841,0)]
  EqualTolerance = true
  ExtensionAngle = 0
  FormatSpec = ⌀%.1w
  FormatSpecOverTolerance = %+.1w
  FormatSpecUnderTolerance = %+.1w
  Inverted = false
  LineAngle = 0
  LockPosition = false
  MeasureType = 1
  OverTolerance = 0
  References2D = -> [View002]
  Rotation = 0
  ScaleType = 0
  TheoreticalExact = false
  Type = 5
  UnderTolerance = 0
  X = 116.2
  Y = 26.2066
FEATURE [TechDraw::DrawViewDimension] Dimension  label="Maß"
  AngleOverride = false
  Arbitrary = false
  ArbitraryTolerances = false
  BoxCorners = (2) [(-121.671,-22.6841,0),(121.671,22.6841,0)]
  EqualTolerance = true
  ExtensionAngle = 0
  FormatSpec = %.1w
  FormatSpecOverTolerance = %+.1w
  FormatSpecUnderTolerance = %+.1w
  Inverted = false
  LineAngle = 0
  LockPosition = false
  MeasureType = 1
  OverTolerance = 0
  References2D = -> [View002]
  Rotation = 0
  ScaleType = 0
  TheoreticalExact = false
  Type = 1
  UnderTolerance = 0
  X = 0
  Y = -33.1174
FEATURE [TechDraw::DrawViewDimension] Dimension006  label="Maß006"
  AngleOverride = false
  Arbitrary = false
  ArbitraryTolerances = false
  BoxCorners = (2) [(-121.671,-22.6841,0),(121.671,22.6841,0)]
  EqualTolerance = true
  ExtensionAngle = 0
  FormatSpec = %.1w
  FormatSpecOverTolerance = %+.1w
  FormatSpecUnderTolerance = %+.1w
  Inverted = false
  LineAngle = 0
  LockPosition = false
  MeasureType = 1
  OverTolerance = 0
  References2D = -> [View002]
  Rotation = 0
  ScaleType = 0
  TheoreticalExact = false
  Type = 1
  UnderTolerance = 0
  X = 130.112
  Y = -23.8998
FEATURE [TechDraw::DrawViewDimension] Dimension007  label="Maß007"
  AngleOverride = false
  Arbitrary = false
  ArbitraryTolerances = false
  BoxCorners = (2) [(-121.671,-22.6841,0),(121.671,22.6841,0)]
  EqualTolerance = true
  ExtensionAngle = 0
  FormatSpec = %.1w
  FormatSpecOverTolerance = %+.1w
  FormatSpecUnderTolerance = %+.1w
  Inverted = false
  LineAngle = 0
  LockPosition = false
  MeasureType = 1
  OverTolerance = 0
  References2D = -> [View002]
  Rotation = 0
  ScaleType = 0
  TheoreticalExact = false
  Type = 1
  UnderTolerance = 0
  X = 129.887
  Y = -14.8303
FEATURE [TechDraw::DrawViewDimension] Dimension008  label="Maß008"
  AngleOverride = false
  Arbitrary = false
  ArbitraryTolerances = false
  BoxCorners = (2) [(-121.671,-22.6841,0),(121.671,22.6841,0)]
  EqualTolerance = true
  ExtensionAngle = 0
  FormatSpec = %.1w
  FormatSpecOverTolerance = %+.1w
  FormatSpecUnderTolerance = %+.1w
  Inverted = false
  LineAngle = 0
  LockPosition = false
  MeasureType = 1
  OverTolerance = 0
  References2D = -> [View002]
  Rotation = 0
  ScaleType = 0
  TheoreticalExact = false
  Type = 1
  UnderTolerance = 0
  X = 88.0393
  Y = -23.8998
FEATURE [TechDraw::DrawViewDimension] Dimension009  label="Maß009"
  AngleOverride = false
  Arbitrary = false
  ArbitraryTolerances = false
  BoxCorners = (2) [(-121.671,-22.6841,0),(121.671,22.6841,0)]
  EqualTolerance = true
  ExtensionAngle = 0
  FormatSpec = %.1w
  FormatSpecOverTolerance = %+.1w
  FormatSpecUnderTolerance = %+.1w
  Inverted = false
  LineAngle = 0
  LockPosition = false
  MeasureType = 1
  OverTolerance = 0
  References2D = -> [View002]
  Rotation = 0
  ScaleType = 0
  TheoreticalExact = false
  Type = 1
  UnderTolerance = 0
  X = 59.7047
  Y = -29.1941
FEATURE [TechDraw::DrawViewDimension] Dimension010  label="Maß010"
  AngleOverride = false
  Arbitrary = false
  ArbitraryTolerances = false
  BoxCorners = (2) [(-121.671,-22.6841,0),(121.671,22.6841,0)]
  EqualTolerance = true
  ExtensionAngle = 0
  FormatSpec = %.1w
  FormatSpecOverTolerance = %+.1w
  FormatSpecUnderTolerance = %+.1w
  Inverted = false
  LineAngle = 0
  LockPosition = false
  MeasureType = 1
  OverTolerance = 0
  References2D = -> [View002]
  Rotation = 0
  ScaleType = 0
  TheoreticalExact = false
  Type = 1
  UnderTolerance = 0
  X = 52.8285
  Y = -5.93466
FEATURE [TechDraw::DrawViewDimension] Dimension011  label="Maß011"
  AngleOverride = false
  Arbitrary = false
  ArbitraryTolerances = false
  BoxCorners = (2) [(-121.671,-22.6841,0),(121.671,22.6841,0)]
  EqualTolerance = true
  ExtensionAngle = 0
  FormatSpec = %.1w
  FormatSpecOverTolerance = %+.1w
  FormatSpecUnderTolerance = %+.1w
  Inverted = false
  LineAngle = 0
  LockPosition = false
  MeasureType = 1
  OverTolerance = 0
  References2D = -> [View002]
  Rotation = 0
  ScaleType = 0
  TheoreticalExact = false
  Type = 1
  UnderTolerance = 0
  X = -26.771
  Y = -5.93466
FEATURE [TechDraw::DrawViewDimension] Dimension012  label="Maß012"
  AngleOverride = false
  Arbitrary = false
  ArbitraryTolerances = false
  BoxCorners = (2) [(-121.671,-22.6841,0),(121.671,22.6841,0)]
  EqualTolerance = true
  ExtensionAngle = 0
  FormatSpec = %.1w
  FormatSpecOverTolerance = %+.1w
  FormatSpecUnderTolerance = %+.1w
  Inverted = false
  LineAngle = 0
  LockPosition = false
  MeasureType = 1
  OverTolerance = 0
  References2D = -> [View002]
  Rotation = 0
  ScaleType = 0
  TheoreticalExact = false
  Type = 1
  UnderTolerance = 0
  X = -114.671
  Y = -5.93466
FEATURE [TechDraw::DrawViewDimension] Dimension013  label="Maß013"
  AngleOverride = false
  Arbitrary = false
  ArbitraryTolerances = false
  BoxCorners = (2) [(-121.671,-22.6841,0),(121.671,22.6841,0)]
  EqualTolerance = true
  ExtensionAngle = 0
  FormatSpec = %.1w
  FormatSpecOverTolerance = %+.1w
  FormatSpecUnderTolerance = %+.1w
  Inverted = false
  LineAngle = 0
  LockPosition = false
  MeasureType = 1
  OverTolerance = 0
  References2D = -> [View002]
  Rotation = 0
  ScaleType = 0
  TheoreticalExact = false
  Type = 2
  UnderTolerance = 0
  X = -135.189
  Y = 0
FEATURE [TechDraw::DrawViewDimension] Dimension014  label="Maß014"
  AngleOverride = false
  Arbitrary = false
  ArbitraryTolerances = false
  BoxCorners = (2) [(-121.671,-22.6841,0),(121.671,22.6841,0)]
  EqualTolerance = true
  ExtensionAngle = 0
  FormatSpec = %.1w
  FormatSpecOverTolerance = %+.1w
  FormatSpecUnderTolerance = %+.1w
  Inverted = false
  LineAngle = 0
  LockPosition = false
  MeasureType = 1
  OverTolerance = 0
  References2D = -> [View002]
  Rotation = 0
  ScaleType = 0
  TheoreticalExact = false
  Type = 2
  UnderTolerance = 0
  X = -135.189
  Y = 18.592
FEATURE [TechDraw::DrawViewDimension] Dimension015  label="Maß015"
  AngleOverride = false
  Arbitrary = false
  ArbitraryTolerances = false
  BoxCorners = (2) [(-121.671,-22.6841,0),(121.671,22.6841,0)]
  EqualTolerance = true
  ExtensionAngle = 0
  FormatSpec = %.2w
  FormatSpecOverTolerance = %+.1w
  FormatSpecUnderTolerance = %+.1w
  Inverted = false
  LineAngle = 0
  LockPosition = false
  MeasureType = 1
  OverTolerance = 0
  References2D = -> [View002]
  Rotation = 0
  ScaleType = 0
  TheoreticalExact = false
  Type = 2
  UnderTolerance = 0
  X = 95.0521
  Y = 0
FEATURE [TechDraw::DrawViewDimension] Dimension016  label="Maß016"
  AngleOverride = false
  Arbitrary = false
  ArbitraryTolerances = false
  BoxCorners = (2) [(-121.671,-27.2635,0),(121.671,27.2635,0)]
  EqualTolerance = true
  ExtensionAngle = 0
  FormatSpec = %.1w
  FormatSpecOverTolerance = %+.1w
  FormatSpecUnderTolerance = %+.1w
  Inverted = false
  LineAngle = 0
  LockPosition = false
  MeasureType = 1
  OverTolerance = 0
  References2D = -> [View003]
  Rotation = 0
  ScaleType = 0
  TheoreticalExact = false
  Type = 1
  UnderTolerance = 0
  X = 79.6078
  Y = 28.7605
FEATURE [TechDraw::DrawViewDimension] Dimension017  label="Maß017"
  AngleOverride = false
  Arbitrary = false
  ArbitraryTolerances = false
  BoxCorners = (2) [(-121.671,-27.2635,0),(121.671,27.2635,0)]
  EqualTolerance = true
  ExtensionAngle = 0
  FormatSpec = %.1w
  FormatSpecOverTolerance = %+.1w
  FormatSpecUnderTolerance = %+.1w
  Inverted = false
  LineAngle = 0
  LockPosition = false
  MeasureType = 1
  OverTolerance = 0
  References2D = -> [View003]
  Rotation = 0
  ScaleType = 0
  TheoreticalExact = false
  Type = 0
  UnderTolerance = 0
  X = 80.0393
  Y = 8.86181
FEATURE [TechDraw::DrawViewDimension] Dimension018  label="Maß018"
  AngleOverride = false
  Arbitrary = false
  ArbitraryTolerances = false
  BoxCorners = (2) [(-121.671,-27.2635,0),(121.671,27.2635,0)]
  EqualTolerance = true
  ExtensionAngle = 0
  FormatSpec = %.1w
  FormatSpecOverTolerance = %+.1w
  FormatSpecUnderTolerance = %+.1w
  Inverted = false
  LineAngle = 0
  LockPosition = false
  MeasureType = 1
  OverTolerance = 0
  References2D = -> [View003]
  Rotation = 0
  ScaleType = 0
  TheoreticalExact = false
  Type = 1
  UnderTolerance = 0
  X = -34.9215
  Y = 17.9828
FEATURE [TechDraw::DrawViewDimension] Dimension019  label="Maß019"
  AngleOverride = false
  Arbitrary = false
  ArbitraryTolerances = false
  BoxCorners = (2) [(-121.671,-27.2635,0),(121.671,27.2635,0)]
  EqualTolerance = true
  ExtensionAngle = 0
  FormatSpec = %.1w
  FormatSpecOverTolerance = %+.1w
  FormatSpecUnderTolerance = %+.1w
  Inverted = false
  LineAngle = 0
  LockPosition = false
  MeasureType = 1
  OverTolerance = 0
  References2D = -> [View003]
  Rotation = 0
  ScaleType = 0
  TheoreticalExact = false
  Type = 0
  UnderTolerance = 0
  X = -116.296
  Y = 17.9828
FEATURE [TechDraw::DrawViewDimension] Dimension020  label="Maß020"
  AngleOverride = false
  Arbitrary = false
  ArbitraryTolerances = false
  BoxCorners = (2) [(-121.671,-27.2635,0),(121.671,27.2635,0)]
  EqualTolerance = true
  ExtensionAngle = 0
  FormatSpec = %.1w
  FormatSpecOverTolerance = %+.1w
  FormatSpecUnderTolerance = %+.1w
  Inverted = false
  LineAngle = 0
  LockPosition = false
  MeasureType = 1
  OverTolerance = 0
  References2D = -> [View003]
  Rotation = 0
  ScaleType = 0
  TheoreticalExact = false
  Type = 0
  UnderTolerance = 0
  X = 46.4535
  Y = 17.9828
FEATURE [TechDraw::DrawViewDimension] Dimension021  label="Maß021"
  AngleOverride = false
  Arbitrary = false
  ArbitraryTolerances = false
  BoxCorners = (2) [(-121.671,-27.2635,0),(121.671,27.2635,0)]
  EqualTolerance = true
  ExtensionAngle = 0
  FormatSpec = R%.1w
  FormatSpecOverTolerance = %+.1w
  FormatSpecUnderTolerance = %+.1w
  Inverted = false
  LineAngle = 0
  LockPosition = false
  MeasureType = 1
  OverTolerance = 0
  References2D = -> [View003]
  Rotation = 0
  ScaleType = 0
  TheoreticalExact = false
  Type = 4
  UnderTolerance = 0
  X = 33.4294
  Y = 17.8156
FEATURE [TechDraw::DrawViewDimension] Dimension022  label="Maß022"
  AngleOverride = false
  Arbitrary = false
  ArbitraryTolerances = false
  BoxCorners = (2) [(-121.671,-27.2635,0),(121.671,27.2635,0)]
  EqualTolerance = true
  ExtensionAngle = 0
  FormatSpec = %.1w
  FormatSpecOverTolerance = %+.1w
  FormatSpecUnderTolerance = %+.1w
  Inverted = false
  LineAngle = 0
  LockPosition = false
  MeasureType = 1
  OverTolerance = 0
  References2D = -> [View003]
  Rotation = 0
  ScaleType = 0
  TheoreticalExact = false
  Type = 0
  UnderTolerance = 0
  X = -135.017
  Y = 23.5135
FEATURE [TechDraw::DrawViewDimension] Dimension023  label="Maß023"
  AngleOverride = false
  Arbitrary = false
  ArbitraryTolerances = false
  BoxCorners = (2) [(-121.671,-27.2635,0),(121.671,27.2635,0)]
  EqualTolerance = true
  ExtensionAngle = 0
  FormatSpec = %.1w
  FormatSpecOverTolerance = %+.1w
  FormatSpecUnderTolerance = %+.1w
  Inverted = false
  LineAngle = 0
  LockPosition = false
  MeasureType = 1
  OverTolerance = 0
  References2D = -> [View003]
  Rotation = 0
  ScaleType = 0
  TheoreticalExact = false
  Type = 2
  UnderTolerance = 0
  X = -135.017
  Y = 7.59205
FEATURE [TechDraw::DrawViewImage] ActiveView001  label="3D"
  Height = 46
  ImageFile = <userpath>/AppData/Local/cache/FreeCAD/Cache/FreeCAD_Doc_ac7c4096-b8b2-46d9-a61c-e3aa69625053_064048_433050/Pag7EC.tmp.png
  LockPosition = true
  Rotation = 0
  Scale = 0.6
  ScaleType = 2
  Width = 90
  X = 55.7509
  Y = 35.1246
FEATURE [TechDraw::DrawPage] Page  label="Mover Stepper Mounts - Dimensions"
  KeepUpdated = true
  NextBalloonIndex = 1
  ProjectionType = 0
  Template = -> Template
  Views = -> [View002,View003,Dimension001,Dimension002,Dimension003,Dimension004,Dimension005,Dimension,Dimension006,Dimension007,Dimension008,Dimension009,Dimension010,Dimension011,Dimension012,Dimension013,Dimension014,Dimension015,Dimension016,Dimension017,Dimension018,Dimension019,Dimension020,Dimension021,Dimension022,Dimension023,ActiveView001]
FEATURE [App::DocumentObjectGroup] Group001  label="Drawings"
  Group = -> [Page001,Page]
FEATURE [Sketcher::SketchObject] Sketch020  label="Sk-Slide Bearing Wascher base"
  ArcFitTolerance = 1e-06
  AttachmentSupport = -> [XY_Plane008]
  FullyConstrained = true
  MakeInternals = false
  MapMode = 5
  sketch-geometry (5):
    g0: Circle CenterX=0 CenterY=0 CenterZ=0 NormalX=0 NormalY=0 NormalZ=1 AngleXU=0 Radius=2.7
    g1: LineSegment StartX=-18 StartY=17 StartZ=0 EndX=-18 EndY=-17 EndZ=0
    g2: LineSegment StartX=-18 StartY=-17 StartZ=0 EndX=18 EndY=-17 EndZ=0
    g3: LineSegment StartX=18 StartY=-17 StartZ=0 EndX=18 EndY=17 EndZ=0
    g4: LineSegment StartX=18 StartY=17 StartZ=0 EndX=-18 EndY=17 EndZ=0
  constraints (12):
    c: Diameter(g0) = 5.4
    c: Coincident(g0,g-1)
    c: Coincident(g1,g2)
    c: Coincident(g2,g3)
    c: Coincident(g3,g4)
    c: Coincident(g4,g1)
    c: Vertical(g1)
    c: Horizontal(g2)
    c: Distance(g1,g3) = 36
    c: Distance(g2,g4) = 34
    c: Symmetric(g3,g1,g-2)
    c: Symmetric(g2,g3,g-1)
FEATURE [PartDesign::Pad] Pad003  label="P-Slide Bearing Washer base"
  Direction = (0,0,1)
  Length = 4
  Length2 = 10
  Profile = -> Sketch020
  ReferenceAxis = -> Sketch020 [N_Axis]
  Refine = true
  Suppressed = false
  Type = 0
FEATURE [PartDesign::Chamfer] Chamfer001  label="P-Slide Bearing Washer Chamfer"
  Angle = 45
  Base = -> Pad003 [Edge10,Edge4]
  BaseFeature = -> Pad003
  ChamferType = 0
  FlipDirection = false
  Refine = true
  Size = 2
  Size2 = 1
  SupportTransform = false
  Suppressed = false
  UseAllEdges = false
FEATURE [PartDesign::Fillet] Fillet001  label="P-Slide Bearing Washer"
  Base = -> Chamfer001 [Edge4,Edge16,Edge1,Edge5]
  BaseFeature = -> Chamfer001
  Radius = 3
  Refine = true
  SupportTransform = false
  Suppressed = false
  UseAllEdges = false
FEATURE [PartDesign::Body] Body005  label="B-Slide Bearing Washer"
  AllowCompound = false
  Group = -> [Sketch020,Pad003,Chamfer001,Fillet001]
  Origin = -> Origin008
  Placement = pos=(106.9,117.1,79.6) rot=(0,0,1;0rad)
  Tip = -> Fillet001
FEATURE [Sketcher::SketchObject] Sketch021  label="Sk-SlideBearingInd_Shaft"
  ArcFitTolerance = 1e-06
  AttachmentSupport = -> [XY_Plane009]
  FullyConstrained = true
  MakeInternals = false
  MapMode = 5
  sketch-geometry (12):
    g0: ArcOfCircle CenterX=-10 CenterY=0 CenterZ=0 NormalX=0 NormalY=0 NormalZ=1 AngleXU=0 Radius=7.7 StartAngle=1.5708 EndAngle=4.71239
    g1: ArcOfCircle CenterX=10 CenterY=2e-16 CenterZ=0 NormalX=0 NormalY=0 NormalZ=1 AngleXU=0 Radius=7.7 StartAngle=4.71239 EndAngle=7.85398
    g2: LineSegment StartX=-10 StartY=7.7 StartZ=0 EndX=10 EndY=7.7 EndZ=0
    g3: LineSegment StartX=-10 StartY=-7.7 StartZ=0 EndX=10 EndY=-7.7 EndZ=0
    g4: ArcOfCircle CenterX=0 CenterY=1 CenterZ=0 NormalX=0 NormalY=0 NormalZ=1 AngleXU=0 Radius=2.7 StartAngle=1e-16 EndAngle=3.14159
    g5: ArcOfCircle CenterX=0 CenterY=-1 CenterZ=0 NormalX=0 NormalY=0 NormalZ=1 AngleXU=0 Radius=2.7 StartAngle=3.14159 EndAngle=6.28319
    g6: LineSegment StartX=2.7 StartY=1 StartZ=0 EndX=2.7 EndY=-1 EndZ=0
    g7: LineSegment StartX=-2.7 StartY=1 StartZ=0 EndX=-2.7 EndY=-1 EndZ=0
    g8: LineSegment [constr] StartX=0 StartY=1 StartZ=0 EndX=0 EndY=0 EndZ=0
    g9: LineSegment [constr] StartX=0 StartY=0 StartZ=0 EndX=0 EndY=-1 EndZ=0
    g10: LineSegment [constr] StartX=-10 StartY=0 StartZ=0 EndX=0 EndY=0 EndZ=0
    g11: LineSegment [constr] StartX=0 StartY=0 StartZ=0 EndX=10 EndY=2e-16 EndZ=0
  constraints (28):
    c: Tangent(g0,g2) = 1.5708
    c: Tangent(g0,g3) = -1.5708
    c: Tangent(g1,g2) = 1.5708
    c: Tangent(g1,g3) = -1.5708
    c: Equal(g0,g1)
    c: Horizontal(g3)
    c: DistanceX(g0,g1) = 20
    c: Coincident(g10,g0)
    c: Coincident(g11,g1)
    c: Tangent(g4,g6) = 1.5708
    c: Tangent(g4,g7) = -1.5708
    c: Tangent(g5,g6) = 1.5708
    c: Tangent(g5,g7) = -1.5708
    c: Equal(g4,g5)
    c: Distance(g4,g5) = 2
    c: Radius(g4) = 2.7
    c: Coincident(g8,g4)
    c: Coincident(g9,g5)
    c: Coincident(g8,g9)
    c: Coincident(g10,g11)
    c: Coincident(g10,g8)
    c: Equal(g10,g11)
    c: Vertical(g8)
    c: Vertical(g9)
    c: Equal(g8,g9)
    c: Coincident(g8,g-1)
    c: Horizontal(g10)
    c: Radius(g1) = 7.7
FEATURE [PartDesign::Pad] Pad004  label="P-SlideBearingInd_Shaft"
  Direction = (0,0,1)
  Length = 2.3
  Length2 = 10
  Profile = -> Sketch021
  ReferenceAxis = -> Sketch021 [N_Axis]
  Refine = true
  Suppressed = false
  Type = 0
FEATURE [Sketcher::SketchObject] Sketch022  label="Sk-SlideBearingInd_Plate"
  ArcFitTolerance = 1e-06
  AttachmentSupport = -> [Pad004]
  ExternalGeometry = -> [Pad004]
  FullyConstrained = true
  MakeInternals = false
  MapMode = 5
  Placement = pos=(0,0,2.3) rot=(0,0,1;0rad)
  sketch-geometry (14):
    g0: ArcOfCircle CenterX=0 CenterY=1 CenterZ=0 NormalX=0 NormalY=0 NormalZ=1 AngleXU=0 Radius=2.7 StartAngle=2.524e-13 EndAngle=3.14159
    g1: ArcOfCircle CenterX=0 CenterY=-1 CenterZ=0 NormalX=0 NormalY=0 NormalZ=1 AngleXU=0 Radius=2.7 StartAngle=3.14159 EndAngle=6.28319
    g2: LineSegment StartX=2.7 StartY=1 StartZ=0 EndX=2.7 EndY=-1 EndZ=0
    g3: LineSegment StartX=-2.7 StartY=1 StartZ=0 EndX=-2.7 EndY=-1 EndZ=0
    g4: LineSegment StartX=-18.7 StartY=-17.7 StartZ=0 EndX=18.7 EndY=-17.7 EndZ=0
    g5: LineSegment StartX=18.7 StartY=-17.7 StartZ=0 EndX=18.7 EndY=17.7 EndZ=0
    g6: LineSegment StartX=18.7 StartY=17.7 StartZ=0 EndX=-18.7 EndY=17.7 EndZ=0
    g7: LineSegment StartX=-18.7 StartY=17.7 StartZ=0 EndX=-18.7 EndY=0 EndZ=0
    g8: LineSegment StartX=-18.7 StartY=0 StartZ=0 EndX=-18.7 EndY=-17.7 EndZ=0
    g9: LineSegment [constr] StartX=-10 StartY=7.7 StartZ=0 EndX=-10 EndY=17.7 EndZ=0
    g10: LineSegment [constr] StartX=-10 StartY=0 StartZ=0 EndX=-17.7 EndY=0 EndZ=0
    g11: LineSegment [constr] StartX=-17.7 StartY=0 StartZ=0 EndX=-18.7 EndY=0 EndZ=0
    g12: LineSegment [constr] StartX=10 StartY=2e-16 StartZ=0 EndX=17.7 EndY=2e-16 EndZ=0
    g13: LineSegment [constr] StartX=17.7 StartY=2e-16 StartZ=0 EndX=18.7 EndY=2e-16 EndZ=0
  constraints (38):
    c: Tangent(g0,g2) = 1.5708
    c: Tangent(g0,g3) = -1.5708
    c: Tangent(g1,g2) = 1.5708
    c: Tangent(g1,g3) = -1.5708
    c: Equal(g0,g1)
    c: Equal(g0,g-3)
    c: Coincident(g0,g-3)
    c: Coincident(g1,g-4)
    c: Vertical(g5)
    c: Horizontal(g4)
    c: Horizontal(g6)
    c: Coincident(g10,g-5)
    c: Coincident(g12,g-6)
    c: Coincident(g7,g8)
    c: Vertical(g7)
    c: Vertical(g8)
    c: Coincident(g7,g11)
    c: Equal(g7,g8)
    c: Coincident(g9,g-5)
    c: PointOnObject(g9,g6)
    c: Vertical(g9)
    c: DistanceY(g9,g9) = 10
    c: Coincident(g10,g11)
    c: Horizontal(g10)
    c: Horizontal(g11)
    c: PointOnObject(g10,g-5)
    c: DistanceX(g11,g11) = 1
    c: PointOnObject(g13,g5)
    c: Coincident(g12,g13)
    c: Horizontal(g12)
    c: Horizontal(g13)
    c: PointOnObject(g12,g-6)
    c: Equal(g11,g13)
    c: DistanceY(g13,g6) = 17.7
    c: Coincident(g7,g6)
    c: Coincident(g8,g4)
    c: Coincident(g5,g4)
    c: Coincident(g5,g6)
FEATURE [PartDesign::Pad] Pad005  label="P-SlideBearingInd_raw"
  BaseFeature = -> Pad004
  Direction = (0,0,1)
  Length = 4
  Length2 = 10
  Profile = -> Sketch022
  ReferenceAxis = -> Sketch022 [N_Axis]
  Refine = true
  Suppressed = false
  Type = 0
FEATURE [PartDesign::Chamfer] Chamfer002  label="P-SlideBearingInd_Chamber"
  Angle = 45
  Base = -> Pad005 [Edge17,Edge18]
  BaseFeature = -> Pad005
  ChamferType = 0
  FlipDirection = false
  Refine = true
  Size = 1
  Size2 = 1
  SupportTransform = false
  Suppressed = false
  UseAllEdges = false
FEATURE [PartDesign::Fillet] Fillet002  label="P-SlideBearingInd_rounded"
  Base = -> Chamfer002 [Edge9,Edge20,Edge18,Edge12]
  BaseFeature = -> Chamfer002
  Radius = 1
  Refine = true
  SupportTransform = false
  Suppressed = false
  UseAllEdges = false
FEATURE [Sketcher::SketchObject] Sketch023  label="Sk-SlideBearing Indicator"
  ArcFitTolerance = 1e-06
  AttachmentSupport = -> [Fillet002]
  ExternalGeometry = -> [Fillet002]
  FullyConstrained = true
  MakeInternals = false
  MapMode = 5
  Placement = pos=(0,-17.7,0) rot=(1,0,0;1.5708rad)
  sketch-geometry (5):
    g0: LineSegment StartX=-10 StartY=2.3 StartZ=0 EndX=0 EndY=2.3 EndZ=0
    g1: LineSegment StartX=0 StartY=2.3 StartZ=0 EndX=10 EndY=2.3 EndZ=0
    g2: ArcOfCircle CenterX=4e-16 CenterY=-4.04091 CenterZ=0 NormalX=0 NormalY=0 NormalZ=1 AngleXU=0 Radius=11.8409 StartAngle=0.56511 EndAngle=2.57648
    g3: GeomPoint X=0 Y=7.8 Z=0
    g4: LineSegment [constr] StartX=0 StartY=7.8 StartZ=0 EndX=0 EndY=2.3 EndZ=0
  constraints (14):
    c: PointOnObject(g0,g-3)
    c: PointOnObject(g1,g-3)
    c: Coincident(g0,g1)
    c: Horizontal(g0)
    c: PointOnObject(g0,g-2)
    c: Equal(g0,g1)
    c: Coincident(g2,g0)
    c: Coincident(g2,g1)
    c: DistanceX(g1,g1) = 10
    c: PointOnObject(g3,g2)
    c: PointOnObject(g3,g-2)
    c: Coincident(g4,g3)
    c: Coincident(g4,g0)
    c: DistanceY(g4,g4) = 5.5
FEATURE [PartDesign::Pad] Pad006  label="P-SlideBearingIndicator"
  BaseFeature = -> Fillet002
  Direction = (0,-1,2e-16)
  Length = 8
  Length2 = 10
  Profile = -> Sketch023
  ReferenceAxis = -> Sketch023 [N_Axis]
  Refine = true
  Suppressed = false
  Type = 0
FEATURE [PartDesign::Body] Body006  label="B-Slide Bearing w. Indicator"
  AllowCompound = false
  Group = -> [Sketch021,Pad004,Sketch022,Pad005,Chamfer002,Fillet002,Sketch023,Pad006]
  Origin = -> Origin009
  Placement = pos=(106.9,117,90) rot=(0,0,1;0rad)
  Tip = -> Pad006
FEATURE [Part::Feature] Part__Feature  label="Microswitch 20mm"
  shape: bbox 53.34 x 10.88 x 20.15 mm, 272 faces (baked)
FEATURE [Part::Feature] Part__Feature001  label="Microswitch 20mm001"
  shape: bbox 3.3 x 1.3 x 2 mm, 8 faces (baked)
FEATURE [Part::Feature] Part__Feature002  label="Microswitch 20mm002"
  shape: bbox 4.6 x 9.15 x 18.7 mm, 30 faces (baked)
FEATURE [Part::Feature] Part__Feature003  label="Microswitch 20mm003"
  shape: bbox 3.1 x 3.6 x 0.5 mm, 9 faces (baked)
FEATURE [Part::Feature] Part__Feature004  label="Microswitch 20mm004"
  shape: bbox 3.1 x 3.6 x 0.5 mm, 9 faces (baked)
FEATURE [Part::Feature] Part__Feature005  label="Microswitch 20mm005"
  shape: bbox 3.1 x 3.6 x 0.5 mm, 9 faces (baked)
FEATURE [Part::Feature] Part__Feature006  label="Microswitch 20mm006"
  shape: bbox 3.4 x 4.979 x 4.979 mm, 6 faces (baked)
FEATURE [App::Part] Microswitch_20mm  label="Microswitch 20mm007"
  Group = -> [Part__Feature,Part__Feature001,Part__Feature002,Part__Feature003,Part__Feature004,Part__Feature005,Part__Feature006]
  Origin = -> Origin010
  Placement = pos=(11.5,25.7,48.7) rot=(0,0,1;1.5708rad)
FEATURE [Sketcher::SketchObject] Sketch024  label="Sk-Switch Bracket Profile"
  ArcFitTolerance = 1e-06
  AttachmentSupport = -> [XY_Plane011]
  FullyConstrained = true
  MakeInternals = false
  MapMode = 5
  sketch-geometry (30):
    g0: LineSegment StartX=4.70711 StartY=1.5 StartZ=0 EndX=4.70711 EndY=-17 EndZ=0
    g1: LineSegment StartX=1.70711 StartY=-20 StartZ=0 EndX=-10.1 EndY=-20 EndZ=0
    g2: LineSegment StartX=-13.1 StartY=-17 StartZ=0 EndX=-13.1 EndY=6 EndZ=0
    g3: LineSegment StartX=-12.1 StartY=7 StartZ=0 EndX=-11.1 EndY=7 EndZ=0
    g4: LineSegment StartX=-11.1 StartY=7 StartZ=0 EndX=-11.1 EndY=-17 EndZ=0
    g5: LineSegment StartX=-10.1 StartY=-18 StartZ=0 EndX=1.70711 EndY=-18 EndZ=0
    g6: LineSegment StartX=0 StartY=-2.5 StartZ=0 EndX=-8.8 EndY=-2.5 EndZ=0
    g7: LineSegment StartX=-8.8 StartY=2.5 StartZ=0 EndX=3.70711 EndY=2.5 EndZ=0
    g8: LineSegment StartX=-8.8 StartY=-2.5 StartZ=0 EndX=-8.8 EndY=0 EndZ=0
    g9: LineSegment StartX=-8.8 StartY=0 StartZ=0 EndX=-8.8 EndY=2.5 EndZ=0
    g10: LineSegment [constr] StartX=-8.8 StartY=0 StartZ=0 EndX=0 EndY=0 EndZ=0
    g11: LineSegment [constr] StartX=0 StartY=-2.5 StartZ=0 EndX=0 EndY=2.5 EndZ=0
    g12: ArcOfCircle CenterX=1.70711 CenterY=-17 CenterZ=0 NormalX=0 NormalY=0 NormalZ=1 AngleXU=0 Radius=3 StartAngle=4.71239 EndAngle=6.28319
    g13: GeomPoint [constr] X=4.70711 Y=-20 Z=0
    g14: ArcOfCircle CenterX=1.70711 CenterY=-17 CenterZ=0 NormalX=0 NormalY=0 NormalZ=1 AngleXU=0 Radius=1 StartAngle=4.71239 EndAngle=6.28319
    g15: ArcOfCircle CenterX=-10.1 CenterY=-17 CenterZ=0 NormalX=0 NormalY=0 NormalZ=1 AngleXU=0 Radius=1 StartAngle=3.14159 EndAngle=4.71239
    g16: ArcOfCircle CenterX=-10.1 CenterY=-17 CenterZ=0 NormalX=0 NormalY=0 NormalZ=1 AngleXU=0 Radius=3 StartAngle=3.14159 EndAngle=4.71239
    g17: GeomPoint [constr] X=-13.1 Y=-20 Z=0
    g18: ArcOfCircle CenterX=3.70711 CenterY=1.5 CenterZ=0 NormalX=0 NormalY=0 NormalZ=1 AngleXU=0 Radius=1 StartAngle=0 EndAngle=1.5708
    g19: GeomPoint [constr] X=4.70711 Y=2.5 Z=0
    g20: ArcOfCircle CenterX=-12.1 CenterY=6 CenterZ=0 NormalX=0 NormalY=0 NormalZ=1 AngleXU=0 Radius=1 StartAngle=1.5708 EndAngle=3.14159
    g21: GeomPoint [constr] X=-13.1 Y=7 Z=0
    g22: LineSegment [constr] StartX=-13.1 StartY=6 StartZ=0 EndX=-11.1 EndY=6 EndZ=0
    g23: LineSegment [constr] StartX=-8.8 StartY=0 StartZ=0 EndX=-11.1 EndY=0 EndZ=0
    g24: LineSegment StartX=2.70711 StartY=-17 StartZ=0 EndX=2.70711 EndY=-5.20711 EndZ=0
    g25: LineSegment StartX=2.41421 StartY=-4.5 StartZ=0 EndX=0.707107 EndY=-2.79289 EndZ=0
    g26: ArcOfCircle CenterX=1.70711 CenterY=-5.20711 CenterZ=0 NormalX=0 NormalY=0 NormalZ=1 AngleXU=0 Radius=1 StartAngle=0 EndAngle=0.785398
    g27: GeomPoint [constr] X=2.70711 Y=-4.79289 Z=0
    g28: ArcOfCircle CenterX=-1.07e-14 CenterY=-3.5 CenterZ=0 NormalX=0 NormalY=0 NormalZ=1 AngleXU=0 Radius=1 StartAngle=0.785398 EndAngle=1.5708
    g29: GeomPoint [constr] X=0 Y=-2.5 Z=0
  constraints (72):
    c: Vertical(g0)
    c: Horizontal(g1)
    c: Vertical(g2)
    c: Horizontal(g3)
    c: Coincident(g3,g4)
    c: Vertical(g4)
    c: Horizontal(g5)
    c: Horizontal(g6)
    c: Coincident(g6,g8)
    c: Coincident(g9,g7)
    c: Horizontal(g7)
    c: DistanceY(g29,g19) = 5
    c: Coincident(g8,g9)
    c: Vertical(g8)
    c: Vertical(g9)
    c: Equal(g8,g9)
    c: Coincident(g10,g8)
    c: Horizontal(g10)
    c: Coincident(g11,g29)
    c: PointOnObject(g11,g7)
    c: Vertical(g11)
    c: PointOnObject(g10,g11)
    c: DistanceX(g10,g10) = 8.8
    c: PointOnObject(g13,g0)
    c: PointOnObject(g13,g1)
    c: Tangent(g0,g12) = 1.5708
    c: Tangent(g1,g12) = 1.5708
    c: Tangent(g5,g14) = -1.5708
    c: Tangent(g4,g15) = -1.5708
    c: Tangent(g5,g15) = -1.5708
    c: PointOnObject(g17,g2)
    c: PointOnObject(g17,g1)
    c: Tangent(g2,g16) = 1.5708
    c: Tangent(g1,g16) = 1.5708
    c: PointOnObject(g19,g7)
    c: PointOnObject(g19,g0)
    c: Tangent(g7,g18) = 1.5708
    c: Tangent(g0,g18) = 1.5708
    c: PointOnObject(g21,g3)
    c: PointOnObject(g21,g2)
    c: Tangent(g3,g20) = 1.5708
    c: Tangent(g2,g20) = 1.5708
    c: Radius(g20) = 1
    c: Equal(g15,g14)
    c: Equal(g20,g15)
    c: Equal(g14,g18)
    c: Coincident(g22,g2)
    c: PointOnObject(g22,g4)
    c: Horizontal(g22)
    c: DistanceX(g22,g22) = 2
    c: Coincident(g16,g15)
    c: Coincident(g14,g12)
    c: DistanceY(g5,g10) = 18
    c: PointOnObject(g23,g4)
    c: Horizontal(g23)
    c: DistanceX(g23,g23) = 2.3
    c: Coincident(g10,g-1)
    c: DistanceY(g23,g3) = 7
    c: Vertical(g24)
    c: PointOnObject(g27,g25)
    c: PointOnObject(g27,g24)
    c: Tangent(g25,g26) = -1.5708
    c: Tangent(g24,g26) = -1.5708
    c: Equal(g26,g18)
    c: DistanceX(g28,g24) = 2
    c: Angle(g24,g25) = 0.785398
    c: Tangent(g6,g28) = -1.5708
    c: Tangent(g25,g28) = -1.5708
    c: Equal(g28,g26)
    c: Tangent(g24,g14) = -1.5708
    c: Coincident(g6,g11)
    c: Coincident(g23,g8)
FEATURE [PartDesign::Pad] Pad007  label="B-Switch Bracket Profile"
  Direction = (0,0,1)
  Length = 22
  Length2 = 10
  Profile = -> Sketch024
  ReferenceAxis = -> Sketch024 [N_Axis]
  Refine = true
  Suppressed = false
  Type = 0
FEATURE [Sketcher::SketchObject] Sketch025  label="Sk-Switch Bracket Pocket"
  ArcFitTolerance = 1e-06
  AttachmentSupport = -> [Pad007]
  FullyConstrained = true
  MakeInternals = false
  MapMode = 5
  Placement = pos=(0,0,0) rot=(1,0,0;3.14159rad)
  sketch-geometry (4):
    g0: LineSegment StartX=-6.8 StartY=-3 StartZ=0 EndX=0 EndY=-3 EndZ=0
    g1: LineSegment StartX=0 StartY=-3 StartZ=0 EndX=0 EndY=3 EndZ=0
    g2: LineSegment StartX=0 StartY=3 StartZ=0 EndX=-6.8 EndY=3 EndZ=0
    g3: LineSegment StartX=-6.8 StartY=3 StartZ=0 EndX=-6.8 EndY=-3 EndZ=0
  constraints (11):
    c: Coincident(g0,g1)
    c: Coincident(g1,g2)
    c: Coincident(g2,g3)
    c: Coincident(g3,g0)
    c: Horizontal(g0)
    c: Horizontal(g2)
    c: Vertical(g1)
    c: Vertical(g3)
    c: DistanceX(g2,g2) = 6.8
    c: DistanceY(g3,g3) = 6
    c: Symmetric(g0,g1,g-1)
FEATURE [PartDesign::Pocket] Pocket  label="P-Switch Bracket Body"
  BaseFeature = -> Pad007
  Direction = (0,0,1)
  Length = 21
  Length2 = 5
  Profile = -> Sketch025
  ReferenceAxis = -> Sketch025 [N_Axis]
  Refine = true
  Suppressed = false
  Type = 0
FEATURE [Sketcher::SketchObject] Sketch026  label="Sk-Switch Bracket Holes"
  ArcFitTolerance = 1e-06
  AttachmentSupport = -> [Pocket]
  ExternalGeometry = -> [Pocket]
  FullyConstrained = true
  MakeInternals = false
  MapMode = 5
  Placement = pos=(4.70711,0,0) rot=(0.57735,0.57735,0.57735;2.0944rad)
  sketch-geometry (4):
    g0: LineSegment [constr] StartX=2.5 StartY=5.2 StartZ=0 EndX=0 EndY=5.2 EndZ=0
    g1: LineSegment [constr] StartX=0 StartY=5.2 StartZ=0 EndX=0 EndY=14.7 EndZ=0
    g2: Circle CenterX=0 CenterY=14.7 CenterZ=0 NormalX=0 NormalY=0 NormalZ=1 AngleXU=0 Radius=1.5
    g3: Circle CenterX=0 CenterY=5.2 CenterZ=0 NormalX=0 NormalY=0 NormalZ=1 AngleXU=0 Radius=1.5
  constraints (11):
    c: Distance(g0) = 2.5
    c: PointOnObject(g0,g-3)
    c: Horizontal(g0)
    c: Coincident(g1,g0)
    c: Vertical(g1)
    c: DistanceY(g1,g1) = 9.5
    c: DistanceY(g-3,g0) = 5.2
    c: Diameter(g2) = 3
    c: Coincident(g2,g1)
    c: Coincident(g3,g0)
    c: Equal(g2,g3)
FEATURE [PartDesign::Pocket] Pocket001  label="P-Switch Bracket drilled"
  BaseFeature = -> Pocket
  Direction = (-1,0,0)
  Length = 5
  Length2 = 5
  Profile = -> Sketch026
  ReferenceAxis = -> Sketch026 [N_Axis]
  Refine = true
  Suppressed = false
  Type = 1
FEATURE [Sketcher::SketchObject] Sketch027  label="Sk-Switch Bracket Nutpockets"
  ArcFitTolerance = 1e-06
  AttachmentSupport = -> [Pocket001]
  ExternalGeometry = -> [Pocket001]
  FullyConstrained = true
  MakeInternals = false
  MapMode = 5
  Placement = pos=(0,0,0) rot=(0.57735,-0.57735,-0.57735;2.0944rad)
  sketch-geometry (14):
    g0: LineSegment StartX=0 StartY=11.64 StartZ=0 EndX=2.65 EndY=13.17 EndZ=0
    g1: LineSegment StartX=2.65 StartY=13.17 StartZ=0 EndX=2.65 EndY=16.23 EndZ=0
    g2: LineSegment StartX=2.65 StartY=16.23 StartZ=0 EndX=-1.927e-13 EndY=17.76 EndZ=0
    g3: LineSegment StartX=-1.927e-13 StartY=17.76 StartZ=0 EndX=-2.65 EndY=16.23 EndZ=0
    g4: LineSegment StartX=-2.65 StartY=16.23 StartZ=0 EndX=-2.65 EndY=13.17 EndZ=0
    g5: LineSegment StartX=-2.65 StartY=13.17 StartZ=0 EndX=0 EndY=11.64 EndZ=0
    g6: Circle [constr] CenterX=0 CenterY=14.7 CenterZ=0 NormalX=0 NormalY=0 NormalZ=1 AngleXU=0 Radius=3.05996
    g7: LineSegment StartX=0 StartY=8.25996 StartZ=0 EndX=-2.65 EndY=6.72998 EndZ=0
    g8: LineSegment StartX=-2.65 StartY=6.72998 StartZ=0 EndX=-2.65 EndY=3.67002 EndZ=0
    g9: LineSegment StartX=-2.65 StartY=3.67002 StartZ=0 EndX=4e-16 EndY=2.14004 EndZ=0
    g10: LineSegment StartX=4e-16 StartY=2.14004 StartZ=0 EndX=2.65 EndY=3.67002 EndZ=0
    g11: LineSegment StartX=2.65 StartY=3.67002 StartZ=0 EndX=2.65 EndY=6.72998 EndZ=0
    g12: LineSegment StartX=2.65 StartY=6.72998 StartZ=0 EndX=0 EndY=8.25996 EndZ=0
    g13: Circle [constr] CenterX=0 CenterY=5.2 CenterZ=0 NormalX=0 NormalY=0 NormalZ=1 AngleXU=0 Radius=3.05996
  constraints (32):
    c: Coincident(g0,g1)
    c: Coincident(g1,g2)
    c: Coincident(g2,g3)
    c: Coincident(g3,g4)
    c: Coincident(g4,g5)
    c: Coincident(g5,g0)
    c: Equal(g0, g1-g5) x5
    c: PointOnObject(g0,g6)
    c: PointOnObject(g1,g6)
    c: PointOnObject(g2,g6)
    c: PointOnObject(g3,g6)
    c: PointOnObject(g4,g6)
    c: PointOnObject(g5,g6)
    c: Coincident(g6,g-3)
    c: PointOnObject(g5,g-2)
    c: Coincident(g7,g8)
    c: Coincident(g8,g9)
    c: Coincident(g9,g10)
    c: Coincident(g10,g11)
    c: Coincident(g11,g12)
    c: Coincident(g12,g7)
    c: Equal(g7, g8-g12) x5
    c: PointOnObject(g7,g13)
    c: PointOnObject(g8,g13)
    c: PointOnObject(g9,g13)
    c: PointOnObject(g10,g13)
    c: PointOnObject(g11,g13)
    c: PointOnObject(g12,g13)
    c: Coincident(g13,g-4)
    c: PointOnObject(g12,g-2)
    c: DistanceX(g3,g1) = 5.3
    c: Equal(g6,g13)
FEATURE [PartDesign::Pocket] Pocket002  label="P-Switch Bracket Nuts"
  BaseFeature = -> Pocket001
  Direction = (1,0,0)
  Length = 2.5
  Length2 = 5
  Profile = -> Sketch027
  ReferenceAxis = -> Sketch027 [N_Axis]
  Refine = true
  Suppressed = false
  Type = 0
FEATURE [Sketcher::SketchObject] Sketch028  label="Sk-Switch Bracket Sinks"
  ArcFitTolerance = 1e-06
  AttachmentSupport = -> [Pocket002]
  ExternalGeometry = -> [Pocket002]
  FullyConstrained = true
  MakeInternals = false
  MapMode = 5
  Placement = pos=(-13.1,0,0) rot=(0.57735,-0.57735,-0.57735;2.0944rad)
  sketch-geometry (2):
    g0: Circle CenterX=0 CenterY=14.7 CenterZ=0 NormalX=0 NormalY=0 NormalZ=1 AngleXU=0 Radius=2.5
    g1: Circle CenterX=0 CenterY=5.2 CenterZ=0 NormalX=0 NormalY=0 NormalZ=1 AngleXU=0 Radius=2.5
  constraints (4):
    c: Diameter(g0) = 5
    c: Coincident(g0,g-3)
    c: Coincident(g1,g-4)
    c: Equal(g1,g0)
FEATURE [PartDesign::Hole] Hole  label="Sk-Switch Bracket"
  BaseFeature = -> Pocket002
  CustomThreadClearance = 0
  Depth = 25
  DepthType = 0
  Diameter = 3
  DrillForDepth = false
  DrillPoint = 1
  DrillPointAngle = 118
  HoleCutCountersinkAngle = 90
  HoleCutCustomValues = false
  HoleCutDepth = 0
  HoleCutDiameter = 5
  HoleCutType = 2
  ModelThread = false
  Profile = -> Sketch028
  Refine = true
  Suppressed = false
  Tapered = false
  TaperedAngle = 90
  ThreadClass = 0
  ThreadDepth = 25
  ThreadDepthType = 0
  ThreadDirection = 0
  ThreadFit = 0
  ThreadSize = 0
  ThreadType = 0
  Threaded = false
  UseCustomThreadClearance = false
FEATURE [PartDesign::Body] Body007  label="B-Switch Bracket"
  AllowCompound = false
  Group = -> [Sketch024,Pad007,Sketch025,Pocket,Sketch026,Pocket001,Sketch027,Pocket002,Sketch028,Hole]
  Origin = -> Origin011
  Placement = pos=(154.5,97.2,-15.5) rot=(-0.57735,-0.57735,-0.57735;4.18879rad)
  Tip = -> Hole
FEATURE [App::DocumentObjectGroup] Group  label="Steppersledge"
  Group = -> [Body001,Body001_Unfold,Body,Body_Unfold,Body004,Body002,Body003,Body006,Body005,Body007]
FEATURE [Mesh::Feature] Mesh  label="M-Mount Washer"
FEATURE [Mesh::Feature] Mesh001  label="M-Slide Bearing"
FEATURE [Mesh::Feature] Mesh002  label="M-Slide Bearing w. Indicator"
FEATURE [Mesh::Feature] Mesh004  label="M-Switch Bracket"
FEATURE [Sketcher::SketchObject] Sketch031  label="Sk-ChairBearing-Profile"
  ArcFitTolerance = 1e-06
  AttachmentSupport = -> [YZ_Plane012]
  FullyConstrained = true
  MakeInternals = false
  MapMode = 5
  Placement = pos=(0,0,0) rot=(0.57735,0.57735,0.57735;2.0944rad)
  sketch-geometry (13):
    g0: LineSegment StartX=0 StartY=0 StartZ=0 EndX=50 EndY=0 EndZ=0
    g1: LineSegment StartX=50 StartY=0 StartZ=0 EndX=50 EndY=14 EndZ=0
    g2: LineSegment StartX=0 StartY=14 StartZ=0 EndX=0 EndY=0 EndZ=0
    g3: Circle CenterX=25 CenterY=14 CenterZ=0 NormalX=0 NormalY=0 NormalZ=1 AngleXU=0 Radius=6.2
    g4: ArcOfCircle CenterX=25 CenterY=14 CenterZ=0 NormalX=0 NormalY=0 NormalZ=1 AngleXU=0 Radius=14 StartAngle=0.125328 EndAngle=3.01626
    g5: LineSegment [constr] StartX=39 StartY=14 StartZ=0 EndX=31.2 EndY=14 EndZ=0
    g6: LineSegment [constr] StartX=31.2 StartY=14 StartZ=0 EndX=11 EndY=14 EndZ=0
    g7: ArcOfCircle [constr] CenterX=25 CenterY=14 CenterZ=0 NormalX=0 NormalY=0 NormalZ=1 AngleXU=0 Radius=14 StartAngle=3.01626 EndAngle=6.40851
    g8: LineSegment StartX=0 StartY=14 StartZ=0 EndX=9.12549 EndY=14 EndZ=0
    g9: LineSegment StartX=50 StartY=14 StartZ=0 EndX=40.8745 EndY=14 EndZ=0
    g10: ArcOfCircle CenterX=9.12549 CenterY=16 CenterZ=0 NormalX=0 NormalY=0 NormalZ=1 AngleXU=0 Radius=2 StartAngle=4.71239 EndAngle=6.15786
    g11: ArcOfCircle CenterX=40.8745 CenterY=16 CenterZ=0 NormalX=0 NormalY=0 NormalZ=1 AngleXU=0 Radius=2 StartAngle=3.26692 EndAngle=4.71239
    g12: LineSegment [constr] StartX=9.12549 StartY=14 StartZ=0 EndX=11 EndY=14 EndZ=0
  constraints (39):
    c: Coincident(g0,g1)
    c: Coincident(g2,g0)
    c: Horizontal(g0)
    c: Vertical(g1)
    c: Vertical(g2)
    c: Distance(g1,g2) = 50
    c: Distance(g0,g2) = 14
    c: Coincident(g0,g-1)
    c: Diameter(g3) = 12.4
    c: Coincident(g4,g3)
    c: Coincident(g5,g6)
    c: Horizontal(g5)
    c: PointOnObject(g5,g3)
    c: DistanceX(g5,g5) = 7.8
    c: DistanceX(g5,g1) = 11
    c: PointOnObject(g7,g6)
    c: Coincident(g4,g7)
    c: Coincident(g8,g2)
    c: Horizontal(g8)
    c: Coincident(g9,g1)
    c: Horizontal(g9)
    c: Equal(g2,g1)
    c: Tangent(g7,g0)
    c: Horizontal(g6)
    c: PointOnObject(g3,g6)
    c: Diameter(g4) = 28
    c: Tangent(g8,g10) = -1.5708
    c: Tangent(g9,g11) = 1.5708
    c: Equal(g10,g11)
    c: Radius(g10) = 2
    c: Equal(g8,g9)
    c: Coincident(g7,g4)
    c: PointOnObject(g6,g7)
    c: PointOnObject(g5,g7)
    c: Tangent(g10,g4) = 1.5708
    c: Tangent(g11,g4) = 1.5708
    c: Coincident(g12,g8)
    c: Coincident(g12,g6)
    c: Tangent(g12,g10)
FEATURE [PartDesign::Pad] Pad008  label="P-ChairBearing Profile"
  Direction = (1,0,0)
  Length = 40
  Length2 = 10
  Placement = pos=(0,0,0) rot=(1,1,1;2.0944rad)
  Profile = -> Sketch031
  ReferenceAxis = -> Sketch031 [N_Axis]
  Refine = true
  Suppressed = false
  Type = 0
FEATURE [Sketcher::SketchObject] Sketch032  label="Sk-ChairBearing Cradle Profile"
  ArcFitTolerance = 1e-06
  AttachmentSupport = -> [Pad008]
  ExternalGeometry = -> [Pad008]
  FullyConstrained = true
  MakeInternals = false
  MapMode = 5
  Placement = pos=(0,0,0) rot=(0.57735,0.57735,-0.57735;2.0944rad)
  sketch-geometry (5):
    g0: LineSegment StartX=0 StartY=1.42e-14 StartZ=0 EndX=-4 EndY=1.42e-14 EndZ=0
    g1: LineSegment StartX=-4.4e-15 StartY=40 StartZ=0 EndX=-4 EndY=40 EndZ=0
    g2: LineSegment StartX=-4.4e-15 StartY=40 StartZ=0 EndX=-4.4e-15 EndY=20 EndZ=0
    g3: LineSegment StartX=-4.4e-15 StartY=20 StartZ=0 EndX=0 EndY=1.42e-14 EndZ=0
    g4: ArcOfCircle CenterX=-52 CenterY=20 CenterZ=0 NormalX=0 NormalY=0 NormalZ=1 AngleXU=0 Radius=52 StartAngle=5.88839 EndAngle=6.67798
  constraints (14):
    c: Coincident(g0,g3)
    c: Horizontal(g0)
    c: Coincident(g1,g2)
    c: Horizontal(g1)
    c: Coincident(g2,g3)
    c: Vertical(g2)
    c: Equal(g2,g3)
    c: Coincident(g4,g1)
    c: Coincident(g4,g0)
    c: Coincident(g-3,g0)
    c: Coincident(g-3,g1)
    c: Equal(g0,g1)
    c: Radius(g4) = 52
    c: DistanceX(g1,g1) = 4
FEATURE [PartDesign::Pocket] Pocket003  label="P-ChairBearing Cradle low"
  BaseFeature = -> Pad008
  Direction = (0,1,0)
  Length = 5
  Length2 = 5
  Placement = pos=(0,0,0) rot=(1,1,1;2.0944rad)
  Profile = -> Sketch032
  ReferenceAxis = -> Sketch032 [N_Axis]
  Refine = true
  Suppressed = false
  Type = 1
FEATURE [Sketcher::SketchObject] Sketch033  label="Sk-ChairBearing-Gradlehole top - old"
  ArcFitTolerance = 1e-06
  AttachmentSupport = -> [Pocket003]
  ExternalGeometry = -> [Pocket003]
  FullyConstrained = true
  MakeInternals = false
  MapMode = 5
  Placement = pos=(0,3.1e-15,14) rot=(0,0,-1;1.5708rad)
  sketch-geometry (15):
    g0: ArcOfCircle CenterX=-44.8745 CenterY=23 CenterZ=0 NormalX=0 NormalY=0 NormalZ=1 AngleXU=0 Radius=3.2 StartAngle=7e-16 EndAngle=3.14159
    g1: ArcOfCircle CenterX=-44.8745 CenterY=17 CenterZ=0 NormalX=0 NormalY=0 NormalZ=1 AngleXU=0 Radius=3.2 StartAngle=3.14159 EndAngle=6.28319
    g2: LineSegment StartX=-41.6745 StartY=23 StartZ=0 EndX=-41.6745 EndY=17 EndZ=0
    g3: LineSegment StartX=-48.0745 StartY=23 StartZ=0 EndX=-48.0745 EndY=17 EndZ=0
    g4: LineSegment [constr] StartX=-40.8745 StartY=7.1e-15 StartZ=0 EndX=-44.8745 EndY=7.1e-15 EndZ=0
    g5: LineSegment [constr] StartX=-40.8745 StartY=40 StartZ=0 EndX=-44.8745 EndY=40 EndZ=0
    g6: LineSegment [constr] StartX=-44.8745 StartY=40 StartZ=0 EndX=-44.8745 EndY=23 EndZ=0
    g7: LineSegment [constr] StartX=-44.8745 StartY=23 StartZ=0 EndX=-44.8745 EndY=17 EndZ=0
    g8: LineSegment [constr] StartX=-44.8745 StartY=17 StartZ=0 EndX=-44.8745 EndY=7.1e-15 EndZ=0
    g9: LineSegment [constr] StartX=-9.12549 StartY=40 StartZ=0 EndX=-5.12549 EndY=40 EndZ=0
    g10: LineSegment [constr] StartX=-5.12549 StartY=40 StartZ=0 EndX=-5.12549 EndY=23 EndZ=0
    g11: ArcOfCircle CenterX=-5.12549 CenterY=23 CenterZ=0 NormalX=0 NormalY=0 NormalZ=1 AngleXU=0 Radius=3.2 StartAngle=0 EndAngle=3.14159
    g12: ArcOfCircle CenterX=-5.12549 CenterY=17 CenterZ=0 NormalX=0 NormalY=0 NormalZ=1 AngleXU=0 Radius=3.2 StartAngle=3.14159 EndAngle=6.28319
    g13: LineSegment StartX=-1.92549 StartY=23 StartZ=0 EndX=-1.92549 EndY=17 EndZ=0
    g14: LineSegment StartX=-8.32549 StartY=23 StartZ=0 EndX=-8.32549 EndY=17 EndZ=0
  constraints (37):
    c: Tangent(g0,g2) = 1.5708
    c: Tangent(g0,g3) = -1.5708
    c: Tangent(g1,g2) = 1.5708
    c: Tangent(g1,g3) = -1.5708
    c: Equal(g0,g1)
    c: Vertical(g2)
    c: Radius(g0) = 3.2
    c: Coincident(g4,g-3)
    c: Coincident(g5,g-3)
    c: Horizontal(g5)
    c: Horizontal(g4)
    c: Coincident(g6,g5)
    c: Coincident(g6,g0)
    c: Vertical(g6)
    c: Coincident(g7,g0)
    c: Coincident(g7,g1)
    c: Coincident(g8,g1)
    c: Coincident(g8,g4)
    c: Vertical(g8)
    c: DistanceX(g5,g5) = 4
    c: Equal(g6,g8)
    c: DistanceY(g7,g7) = 6
    c: Coincident(g9,g-4)
    c: Horizontal(g9)
    c: Coincident(g10,g9)
    c: Vertical(g10)
    c: Equal(g5,g9)
    c: Equal(g6,g10)
    c: Tangent(g11,g13) = 1.5708
    c: Tangent(g11,g14) = -1.5708
    c: Tangent(g12,g13) = 1.5708
    c: Tangent(g12,g14) = -1.5708
    c: Equal(g11,g12)
    c: Coincident(g11,g10)
    c: Vertical(g13)
    c: Equal(g2,g14)
    c: Equal(g0,g11)
FEATURE [Sketcher::SketchObject] Sketch034  label="Sk-ChairBearing-Gradlehole btm"
  ArcFitTolerance = 1e-06
  AttachmentOffset = pos=(0,0,-10) rot=(0,0,1;0rad)
  AttachmentSupport = -> [Pocket003]
  ExternalGeometry = -> [Pocket003]
  FullyConstrained = true
  MakeInternals = false
  MapMode = 5
  Placement = pos=(0,3.1e-15,4) rot=(0,0,-1;1.5708rad)
  sketch-geometry (15):
    g0: ArcOfCircle CenterX=-44.8745 CenterY=24 CenterZ=0 NormalX=0 NormalY=0 NormalZ=1 AngleXU=0 Radius=3.2 StartAngle=6e-16 EndAngle=3.14159
    g1: ArcOfCircle CenterX=-44.8745 CenterY=16 CenterZ=0 NormalX=0 NormalY=0 NormalZ=1 AngleXU=0 Radius=3.2 StartAngle=3.14159 EndAngle=6.28319
    g2: LineSegment StartX=-41.6745 StartY=24 StartZ=0 EndX=-41.6745 EndY=16 EndZ=0
    g3: LineSegment StartX=-48.0745 StartY=24 StartZ=0 EndX=-48.0745 EndY=16 EndZ=0
    g4: LineSegment [constr] StartX=-40.8745 StartY=7.1e-15 StartZ=0 EndX=-44.8745 EndY=7.1e-15 EndZ=0
    g5: LineSegment [constr] StartX=-40.8745 StartY=40 StartZ=0 EndX=-44.8745 EndY=40 EndZ=0
    g6: LineSegment [constr] StartX=-44.8745 StartY=40 StartZ=0 EndX=-44.8745 EndY=24 EndZ=0
    g7: LineSegment [constr] StartX=-44.8745 StartY=24 StartZ=0 EndX=-44.8745 EndY=16 EndZ=0
    g8: LineSegment [constr] StartX=-44.8745 StartY=16 StartZ=0 EndX=-44.8745 EndY=7.1e-15 EndZ=0
    g9: LineSegment [constr] StartX=-9.12549 StartY=40 StartZ=0 EndX=-5.12549 EndY=40 EndZ=0
    g10: LineSegment [constr] StartX=-5.12549 StartY=40 StartZ=0 EndX=-5.12549 EndY=24 EndZ=0
    g11: ArcOfCircle CenterX=-5.12549 CenterY=24 CenterZ=0 NormalX=0 NormalY=0 NormalZ=1 AngleXU=0 Radius=3.2 StartAngle=0 EndAngle=3.14159
    g12: ArcOfCircle CenterX=-5.12549 CenterY=16 CenterZ=0 NormalX=0 NormalY=0 NormalZ=1 AngleXU=0 Radius=3.2 StartAngle=3.14159 EndAngle=6.28319
    g13: LineSegment StartX=-1.92549 StartY=24 StartZ=0 EndX=-1.92549 EndY=16 EndZ=0
    g14: LineSegment StartX=-8.32549 StartY=24 StartZ=0 EndX=-8.32549 EndY=16 EndZ=0
  constraints (37):
    c: Tangent(g0,g2) = 1.5708
    c: Tangent(g0,g3) = -1.5708
    c: Tangent(g1,g2) = 1.5708
    c: Tangent(g1,g3) = -1.5708
    c: Equal(g0,g1)
    c: Vertical(g2)
    c: Radius(g0) = 3.2
    c: Coincident(g4,g-3)
    c: Coincident(g5,g-3)
    c: Horizontal(g5)
    c: Horizontal(g4)
    c: Coincident(g6,g5)
    c: Coincident(g6,g0)
    c: Vertical(g6)
    c: Coincident(g7,g0)
    c: Coincident(g7,g1)
    c: Coincident(g8,g1)
    c: Coincident(g8,g4)
    c: Vertical(g8)
    c: DistanceX(g5,g5) = 4
    c: Equal(g6,g8)
    c: DistanceY(g7,g7) = 8
    c: Coincident(g9,g-4)
    c: Horizontal(g9)
    c: Coincident(g10,g9)
    c: Vertical(g10)
    c: Equal(g5,g9)
    c: Equal(g6,g10)
    c: Tangent(g11,g13) = 1.5708
    c: Tangent(g11,g14) = -1.5708
    c: Tangent(g12,g13) = 1.5708
    c: Tangent(g12,g14) = -1.5708
    c: Equal(g11,g12)
    c: Coincident(g11,g10)
    c: Vertical(g13)
    c: Equal(g2,g14)
    c: Equal(g0,g11)
FEATURE [Sketcher::SketchObject] Sketch035  label="Sk-ChairBearing-Gradlehole top"
  ArcFitTolerance = 1e-06
  AttachmentSupport = -> [Pocket003]
  ExternalGeometry = -> [Sketch033]
  FullyConstrained = true
  MakeInternals = false
  MapMode = 5
  Placement = pos=(0,3.1e-15,14) rot=(0,0,-1;1.5708rad)
  sketch-geometry (17):
    g0: LineSegment [constr] StartX=-44.8745 StartY=23 StartZ=0 EndX=-44.8745 EndY=20 EndZ=0
    g1: LineSegment [constr] StartX=-44.8745 StartY=20 StartZ=0 EndX=-44.8745 EndY=17 EndZ=0
    g2: LineSegment [constr] StartX=-44.8745 StartY=20 StartZ=0 EndX=-5.12549 EndY=20 EndZ=0
    g3: LineSegment [constr] StartX=-5.12549 StartY=20 StartZ=0 EndX=-5.12549 EndY=23 EndZ=0
    g4: Circle [constr] CenterX=-44.8745 CenterY=20 CenterZ=0 NormalX=0 NormalY=0 NormalZ=1 AngleXU=0 Radius=3.2
    g5: Circle [constr] CenterX=-5.12549 CenterY=20 CenterZ=0 NormalX=0 NormalY=0 NormalZ=1 AngleXU=0 Radius=3.2
    g6: Ellipse CenterX=-44.8745 CenterY=20 CenterZ=0 NormalX=0 NormalY=0 NormalZ=1 MajorRadius=3.4 MinorRadius=3.2 AngleXU=1.5708
    g7: LineSegment [constr] StartX=-44.8745 StartY=23.4 StartZ=0 EndX=-44.8745 EndY=16.6 EndZ=0
    g8: LineSegment [constr] StartX=-48.0745 StartY=20 StartZ=0 EndX=-41.6745 EndY=20 EndZ=0
    g9: GeomPoint [constr] X=-44.8745 Y=21.1489 Z=0
    g10: GeomPoint [constr] X=-44.8745 Y=18.8511 Z=0
    g11: Ellipse CenterX=-5.12549 CenterY=20 CenterZ=0 NormalX=0 NormalY=0 NormalZ=1 MajorRadius=3.4 MinorRadius=3.2 AngleXU=1.5708
    g12: LineSegment [constr] StartX=-5.12549 StartY=23.4 StartZ=0 EndX=-5.12549 EndY=16.6 EndZ=0
    g13: LineSegment [constr] StartX=-8.32549 StartY=20 StartZ=0 EndX=-1.92549 EndY=20 EndZ=0
    g14: GeomPoint [constr] X=-5.12549 Y=21.1489 Z=0
    g15: GeomPoint [constr] X=-5.12549 Y=18.8511 Z=0
    g16: LineSegment [constr] StartX=-44.8745 StartY=23.4 StartZ=0 EndX=-5.12549 EndY=23.4 EndZ=0
  constraints (26):
    c: Coincident(g0,g-3)
    c: Vertical(g0)
    c: Coincident(g1,g0)
    c: Coincident(g1,g-4)
    c: Equal(g1,g0)
    c: Coincident(g2,g0)
    c: Horizontal(g2)
    c: Coincident(g3,g2)
    c: Coincident(g3,g-5)
    c: Vertical(g3)
    c: Coincident(g4,g0)
    c: Coincident(g5,g2)
    c: Equal(g4,g5)
    c: Equal(g4,g-3)
    c: InternalAlignment(g7-g10 -> g6) x4
    c: Coincident(g6,g0)
    c: PointOnObject(g8,g-6)
    c: InternalAlignment(g12-g15 -> g11) x4
    c: Coincident(g11,g2)
    c: PointOnObject(g13,g-7)
    c: Horizontal(g16)
    c: Coincident(g12,g16)
    c: Coincident(g16,g7)
    c: Vertical(g7)
    c: Vertical(g12)
    c: DistanceY(g7,g7) = 6.8
FEATURE [Sketcher::SketchObject] Sketch036  label="Sk-ChairBearing Cradle Upper Profile front"
  ArcFitTolerance = 1e-06
  AttachmentSupport = -> [Pocket003]
  ExternalGeometry = -> [Pad008]
  FullyConstrained = true
  MakeInternals = false
  MapMode = 5
  Placement = pos=(0,0,0) rot=(0.57735,0.57735,-0.57735;2.0944rad)
  sketch-geometry (5):
    g0: LineSegment StartX=0 StartY=1.42e-14 StartZ=0 EndX=-9 EndY=1.42e-14 EndZ=0
    g1: LineSegment StartX=-4.4e-15 StartY=40 StartZ=0 EndX=-9 EndY=40 EndZ=0
    g2: LineSegment StartX=-4.4e-15 StartY=40 StartZ=0 EndX=-4.4e-15 EndY=20 EndZ=0
    g3: LineSegment StartX=-4.4e-15 StartY=20 StartZ=0 EndX=0 EndY=1.42e-14 EndZ=0
    g4: ArcOfCircle CenterX=-57 CenterY=20 CenterZ=0 NormalX=0 NormalY=0 NormalZ=1 AngleXU=0 Radius=52 StartAngle=5.88839 EndAngle=6.67798
  constraints (14):
    c: Coincident(g0,g3)
    c: Horizontal(g0)
    c: Coincident(g1,g2)
    c: Horizontal(g1)
    c: Coincident(g2,g3)
    c: Vertical(g2)
    c: Equal(g2,g3)
    c: Coincident(g4,g1)
    c: Coincident(g4,g0)
    c: Coincident(g-3,g0)
    c: Coincident(g-3,g1)
    c: Equal(g0,g1)
    c: Radius(g4) = 52
    c: DistanceX(g1,g1) = 9
FEATURE [PartDesign::Pocket] Pocket004  label="P-ChairBearing Cradle inset front"
  BaseFeature = -> Pocket003
  Direction = (0,1,0)
  Length = 16
  Length2 = 5
  Placement = pos=(0,0,0) rot=(1,1,1;2.0944rad)
  Profile = -> Sketch036
  ReferenceAxis = -> Sketch036 [N_Axis]
  Refine = true
  Suppressed = false
  Type = 0
FEATURE [Sketcher::SketchObject] Sketch037  label="Sk-ChairBearing Cradle Upper Profile rear"
  ArcFitTolerance = 1e-06
  AttachmentSupport = -> [Pocket004]
  ExternalGeometry = -> [Pad008]
  FullyConstrained = true
  MakeInternals = false
  MapMode = 5
  Placement = pos=(1.1e-14,50,0) rot=(0.57735,0.57735,0.57735;4.18879rad)
  sketch-geometry (5):
    g0: LineSegment StartX=3.89e-14 StartY=0 StartZ=0 EndX=9 EndY=0 EndZ=0
    g1: LineSegment StartX=4.33e-14 StartY=40 StartZ=0 EndX=9 EndY=40 EndZ=0
    g2: LineSegment StartX=4.33e-14 StartY=40 StartZ=0 EndX=4.33e-14 EndY=20 EndZ=0
    g3: LineSegment StartX=4.33e-14 StartY=20 StartZ=0 EndX=3.89e-14 EndY=0 EndZ=0
    g4: ArcOfCircle CenterX=57 CenterY=20 CenterZ=0 NormalX=0 NormalY=0 NormalZ=1 AngleXU=0 Radius=52 StartAngle=2.7468 EndAngle=3.53638
  constraints (14):
    c: Coincident(g0,g3)
    c: Horizontal(g0)
    c: Coincident(g1,g2)
    c: Horizontal(g1)
    c: Coincident(g2,g3)
    c: Vertical(g2)
    c: Equal(g2,g3)
    c: Coincident(g-3,g0)
    c: Coincident(g-3,g1)
    c: Equal(g0,g1)
    c: DistanceX(g1,g1) = 9
    c: Coincident(g4,g1)
    c: Coincident(g4,g0)
    c: Radius(g4) = 52
FEATURE [PartDesign::Pocket] Pocket005  label="P-ChairBearing Cradle"
  BaseFeature = -> Pocket004
  Direction = (0,-1,0)
  Length = 16
  Length2 = 5
  Placement = pos=(0,0,0) rot=(1,1,1;2.0944rad)
  Profile = -> Sketch037
  ReferenceAxis = -> Sketch037 [N_Axis]
  Refine = true
  Suppressed = false
  Type = 0
FEATURE [PartDesign::SubtractiveLoft] SubtractiveLoft  label="P-ChairBearing drilled"
  BaseFeature = -> Pocket005
  Closed = false
  Placement = pos=(0,0,0) rot=(1,1,1;2.0944rad)
  Profile = -> Sketch035
  Refine = true
  Ruled = false
  Sections = -> [Sketch034]
  Suppressed = false
FEATURE [PartDesign::Body] Body008  label="B-ChairBearing rear"
  AllowCompound = false
  Group = -> [Sketch031,Pad008,Sketch032,Pocket003,Sketch033,Sketch034,Sketch035,Sketch036,Sketch037,Pocket004,Pocket005,SubtractiveLoft]
  Origin = -> Origin012
  Tip = -> SubtractiveLoft
FEATURE [App::DocumentObjectGroup] Group003  label="ChairBearings"
  Group = -> [Body008]
FEATURE [Mesh::Feature] Mesh005  label="M-ChairBearing rear"
FEATURE [Mesh::Feature] Mesh006  label="M-Slide Bearing Washer"
FEATURE [App::DocumentObjectGroup] Group002  label="Meshes"
  Group = -> [Mesh,Mesh002,Mesh001,Mesh006,Mesh004,Mesh005]
note: 2 file-system paths scrubbed to <path> (originals preserved in the JSON sidecar)
